FCSTD DOCUMENT  (FreeCAD 0.18R16131 (Git))
Label: Ladeflaeche
License: All rights reserved
LicenseURL: http://en.wikipedia.org/wiki/All_rights_reserved
objects: App::Part×3, Sketcher::SketchObject×3
note: 3 computed .brp shape members not serialized (recipe doc carries the construction recipe); baked Part::Feature solids carry a one-line shape summary decoded from their .brp

FEATURE [App::Part] Part
  Origin = -> Origin
FEATURE [Sketcher::SketchObject] Sketch
  sketch-geometry (292):
    g0: LineSegment StartX=-33.845 StartY=32.8586 StartZ=0 EndX=-13.845 EndY=32.8586 EndZ=0
    g1: LineSegment StartX=-33.845 StartY=32.8586 StartZ=0 EndX=-33.845 EndY=29.8586 EndZ=0
    g2: LineSegment StartX=-33.845 StartY=29.8586 StartZ=0 EndX=-43.845 EndY=29.8586 EndZ=0
    g3: LineSegment StartX=-43.845 StartY=29.8586 StartZ=0 EndX=-43.845 EndY=19.8586 EndZ=0
    g4: LineSegment StartX=-43.845 StartY=19.8586 StartZ=0 EndX=-33.845 EndY=19.8586 EndZ=0
    g5: LineSegment StartX=-33.845 StartY=19.8586 StartZ=0 EndX=-33.845 EndY=6.85863 EndZ=0
    g6: LineSegment StartX=-33.845 StartY=6.85863 StartZ=0 EndX=-13.845 EndY=6.85863 EndZ=0
    g7: LineSegment StartX=-13.845 StartY=6.85863 StartZ=0 EndX=-13.845 EndY=19.8586 EndZ=0
    g8: LineSegment StartX=-13.845 StartY=19.8586 StartZ=0 EndX=-3.84503 EndY=19.8586 EndZ=0
    g9: LineSegment StartX=-3.84503 StartY=19.8586 StartZ=0 EndX=-3.84503 EndY=29.8586 EndZ=0
    g10: LineSegment StartX=-3.84503 StartY=29.8586 StartZ=0 EndX=-13.845 EndY=29.8586 EndZ=0
    g11: LineSegment StartX=-13.845 StartY=29.8586 StartZ=0 EndX=-13.845 EndY=32.8586 EndZ=0
    g12: LineSegment StartX=-259.768 StartY=205.25 StartZ=0 EndX=-259.768 EndY=208.25 EndZ=0
    g13: LineSegment StartX=-259.768 StartY=208.25 StartZ=0 EndX=-219.768 EndY=208.25 EndZ=0
    g14: LineSegment StartX=-219.768 StartY=208.25 StartZ=0 EndX=-219.768 EndY=205.25 EndZ=0
    g15: LineSegment StartX=-219.768 StartY=205.25 StartZ=0 EndX=-179.768 EndY=205.25 EndZ=0
    g16: LineSegment StartX=-179.768 StartY=205.25 StartZ=0 EndX=-179.768 EndY=208.25 EndZ=0
    g17: LineSegment StartX=-179.768 StartY=208.25 StartZ=0 EndX=-139.768 EndY=208.25 EndZ=0
    g18: LineSegment StartX=-139.768 StartY=208.25 StartZ=0 EndX=-139.768 EndY=205.25 EndZ=0
    g19: LineSegment StartX=-139.768 StartY=205.25 StartZ=0 EndX=-99.7679 EndY=205.25 EndZ=0
    g20: LineSegment StartX=-99.7679 StartY=205.25 StartZ=0 EndX=-99.7679 EndY=208.25 EndZ=0
    g21: LineSegment StartX=-99.7679 StartY=208.25 StartZ=0 EndX=-59.7679 EndY=208.25 EndZ=0
    g22: LineSegment StartX=-59.7679 StartY=208.25 StartZ=0 EndX=-59.7679 EndY=205.25 EndZ=0
    g23: LineSegment StartX=-259.768 StartY=205.25 StartZ=0 EndX=-256.768 EndY=205.25 EndZ=0
    g24: LineSegment StartX=-256.768 StartY=205.25 StartZ=0 EndX=-256.768 EndY=175.25 EndZ=0
    g25: LineSegment StartX=-256.768 StartY=175.25 StartZ=0 EndX=-259.768 EndY=175.25 EndZ=0
    g26: LineSegment StartX=-259.768 StartY=175.25 StartZ=0 EndX=-259.768 EndY=145.25 EndZ=0
    g27: LineSegment StartX=-59.7679 StartY=205.25 StartZ=0 EndX=-62.7679 EndY=205.25 EndZ=0
    g28: LineSegment StartX=-62.7679 StartY=205.25 StartZ=0 EndX=-62.7679 EndY=175.25 EndZ=0
    g29: LineSegment StartX=-62.7679 StartY=175.25 StartZ=0 EndX=-59.7679 EndY=175.25 EndZ=0
    g30: LineSegment StartX=-59.7679 StartY=175.25 StartZ=0 EndX=-59.7679 EndY=145.25 EndZ=0
    g31: LineSegment StartX=-259.768 StartY=145.25 StartZ=0 EndX=-256.768 EndY=145.25 EndZ=0
    g32: LineSegment StartX=-256.768 StartY=145.25 StartZ=0 EndX=-256.768 EndY=115.25 EndZ=0
    g33: LineSegment StartX=-256.768 StartY=115.25 StartZ=0 EndX=-259.768 EndY=115.25 EndZ=0
    g34: LineSegment StartX=-259.768 StartY=115.25 StartZ=0 EndX=-259.768 EndY=93.2502 EndZ=0
    g35: LineSegment StartX=-259.768 StartY=93.2502 StartZ=0 EndX=-256.768 EndY=93.2502 EndZ=0
    g36: LineSegment StartX=-256.768 StartY=93.2502 StartZ=0 EndX=-256.768 EndY=63.2502 EndZ=0
    g37: LineSegment StartX=-256.768 StartY=63.2502 StartZ=0 EndX=-259.768 EndY=63.2502 EndZ=0
    g38: LineSegment StartX=-259.768 StartY=63.2502 StartZ=0 EndX=-259.768 EndY=30.1502 EndZ=0
    g39: LineSegment StartX=-259.768 StartY=30.1502 StartZ=0 EndX=-219.768 EndY=30.1502 EndZ=0
    g40: LineSegment StartX=-219.768 StartY=30.1502 StartZ=0 EndX=-219.768 EndY=33.1502 EndZ=0
    g41: LineSegment StartX=-219.768 StartY=33.1502 StartZ=0 EndX=-179.768 EndY=33.1502 EndZ=0
    g42: LineSegment StartX=-179.768 StartY=33.1502 StartZ=0 EndX=-179.768 EndY=30.1502 EndZ=0
    g43: LineSegment StartX=-179.768 StartY=30.1502 StartZ=0 EndX=-139.768 EndY=30.1502 EndZ=0
    g44: LineSegment StartX=-139.768 StartY=30.1502 StartZ=0 EndX=-139.768 EndY=33.1502 EndZ=0
    g45: LineSegment StartX=-139.768 StartY=33.1502 StartZ=0 EndX=-99.7679 EndY=33.1502 EndZ=0
    g46: LineSegment StartX=-99.7679 StartY=33.1502 StartZ=0 EndX=-99.7679 EndY=30.1502 EndZ=0
    g47: LineSegment StartX=-99.7679 StartY=30.1502 StartZ=0 EndX=-59.7679 EndY=30.1502 EndZ=0
    g48: LineSegment StartX=-59.7679 StartY=30.1502 StartZ=0 EndX=-59.7679 EndY=63.2502 EndZ=0
    g49: LineSegment StartX=-59.7679 StartY=63.2502 StartZ=0 EndX=-62.7679 EndY=63.2502 EndZ=0
    g50: LineSegment StartX=-62.7679 StartY=63.2502 StartZ=0 EndX=-62.7679 EndY=93.2502 EndZ=0
    g51: LineSegment StartX=-62.7679 StartY=93.2502 StartZ=0 EndX=-59.7679 EndY=93.2502 EndZ=0
    g52: LineSegment StartX=-59.7679 StartY=93.2502 StartZ=0 EndX=-59.7679 EndY=115.25 EndZ=0
    g53: LineSegment StartX=-59.7679 StartY=115.25 StartZ=0 EndX=-62.7679 EndY=115.25 EndZ=0
    g54: LineSegment StartX=-62.7679 StartY=115.25 StartZ=0 EndX=-62.7679 EndY=145.25 EndZ=0
    g55: LineSegment StartX=-62.7679 StartY=145.25 StartZ=0 EndX=-59.7679 EndY=145.25 EndZ=0
    g56: LineSegment StartX=-239.768 StartY=198.25 StartZ=0 EndX=-219.768 EndY=198.25 EndZ=0
    g57: LineSegment StartX=-239.768 StartY=198.25 StartZ=0 EndX=-239.768 EndY=195.15 EndZ=0
    g58: LineSegment StartX=-219.768 StartY=198.25 StartZ=0 EndX=-219.768 EndY=195.15 EndZ=0
    g59: LineSegment StartX=-239.768 StartY=195.15 StartZ=0 EndX=-219.768 EndY=195.15 EndZ=0
    g60: LineSegment StartX=-99.7679 StartY=198.25 StartZ=0 EndX=-99.7679 EndY=195.15 EndZ=0
    g61: LineSegment StartX=-99.7679 StartY=198.25 StartZ=0 EndX=-79.7679 EndY=198.25 EndZ=0
    g62: LineSegment StartX=-79.7679 StartY=198.25 StartZ=0 EndX=-79.7679 EndY=195.15 EndZ=0
    g63: LineSegment StartX=-99.7679 StartY=195.15 StartZ=0 EndX=-79.7679 EndY=195.15 EndZ=0
    g64: LineSegment StartX=-239.768 StartY=48.2502 StartZ=0 EndX=-219.768 EndY=48.2502 EndZ=0
    g65: LineSegment StartX=-219.768 StartY=48.2502 StartZ=0 EndX=-219.768 EndY=51.3502 EndZ=0
    g66: LineSegment StartX=-219.768 StartY=51.3502 StartZ=0 EndX=-239.768 EndY=51.3502 EndZ=0
    g67: LineSegment StartX=-239.768 StartY=48.2502 StartZ=0 EndX=-239.768 EndY=51.3502 EndZ=0
    g68: LineSegment StartX=-99.7679 StartY=48.2502 StartZ=0 EndX=-79.7679 EndY=48.2502 EndZ=0
    g69: LineSegment StartX=-79.7679 StartY=48.2502 StartZ=0 EndX=-79.7679 EndY=45.1502 EndZ=0
    g70: LineSegment StartX=-79.7679 StartY=45.1502 StartZ=0 EndX=-99.7679 EndY=45.1502 EndZ=0
    g71: LineSegment StartX=-99.7679 StartY=48.2502 StartZ=0 EndX=-99.7679 EndY=45.1502 EndZ=0
    g72: LineSegment StartX=-239.768 StartY=105.15 StartZ=0 EndX=-219.768 EndY=105.15 EndZ=0
    g73: LineSegment StartX=-239.768 StartY=105.15 StartZ=0 EndX=-239.768 EndY=108.25 EndZ=0
    g74: LineSegment StartX=-239.768 StartY=108.25 StartZ=0 EndX=-219.768 EndY=108.25 EndZ=0
    g75: LineSegment StartX=-219.768 StartY=108.25 StartZ=0 EndX=-219.768 EndY=105.15 EndZ=0
    g76: LineSegment StartX=-99.7679 StartY=105.15 StartZ=0 EndX=-99.7679 EndY=108.25 EndZ=0
    g77: LineSegment StartX=-99.7679 StartY=108.25 StartZ=0 EndX=-79.7679 EndY=108.25 EndZ=0
    g78: LineSegment StartX=-79.7679 StartY=108.25 StartZ=0 EndX=-79.7679 EndY=105.15 EndZ=0
    g79: LineSegment StartX=-99.7679 StartY=105.15 StartZ=0 EndX=-79.7679 EndY=105.15 EndZ=0
    g80: LineSegment StartX=-209.768 StartY=175.25 StartZ=0 EndX=-169.768 EndY=175.25 EndZ=0
    g81: LineSegment StartX=-209.768 StartY=175.25 StartZ=0 EndX=-209.768 EndY=172.25 EndZ=0
    g82: LineSegment StartX=-209.768 StartY=172.25 StartZ=0 EndX=-169.768 EndY=172.25 EndZ=0
    g83: LineSegment StartX=-169.768 StartY=175.25 StartZ=0 EndX=-169.768 EndY=172.25 EndZ=0
    g84: LineSegment StartX=-149.768 StartY=175.25 StartZ=0 EndX=-149.768 EndY=172.25 EndZ=0
    g85: LineSegment StartX=-149.768 StartY=175.25 StartZ=0 EndX=-109.768 EndY=175.25 EndZ=0
    g86: LineSegment StartX=-109.768 StartY=175.25 StartZ=0 EndX=-109.768 EndY=172.25 EndZ=0
    g87: LineSegment StartX=-149.768 StartY=172.25 StartZ=0 EndX=-109.768 EndY=172.25 EndZ=0
    g88: LineSegment StartX=-232.768 StartY=93.2502 StartZ=0 EndX=-229.768 EndY=93.2502 EndZ=0
    g89: LineSegment StartX=-232.768 StartY=93.2502 StartZ=0 EndX=-232.768 EndY=63.2502 EndZ=0
    g90: LineSegment StartX=-232.768 StartY=63.2502 StartZ=0 EndX=-229.768 EndY=63.2502 EndZ=0
    g91: LineSegment StartX=-229.768 StartY=93.2502 StartZ=0 EndX=-229.768 EndY=63.2502 EndZ=0
    g92: LineSegment StartX=-232.768 StartY=145.25 StartZ=0 EndX=-232.768 EndY=115.25 EndZ=0
    g93: LineSegment StartX=-232.768 StartY=115.25 StartZ=0 EndX=-229.768 EndY=115.25 EndZ=0
    g94: LineSegment StartX=-229.768 StartY=145.25 StartZ=0 EndX=-229.768 EndY=115.25 EndZ=0
    g95: LineSegment StartX=-232.768 StartY=145.25 StartZ=0 EndX=-229.768 EndY=145.25 EndZ=0
    g96: LineSegment StartX=-89.7679 StartY=145.25 StartZ=0 EndX=-89.7679 EndY=115.25 EndZ=0
    g97: LineSegment StartX=-89.7679 StartY=145.25 StartZ=0 EndX=-86.7679 EndY=145.25 EndZ=0
    g98: LineSegment StartX=-86.7679 StartY=145.25 StartZ=0 EndX=-86.7679 EndY=115.25 EndZ=0
    g99: LineSegment StartX=-89.7679 StartY=115.25 StartZ=0 EndX=-86.7679 EndY=115.25 EndZ=0
    g100: LineSegment StartX=-89.7679 StartY=93.2502 StartZ=0 EndX=-89.7679 EndY=63.2502 EndZ=0
    g101: LineSegment StartX=-89.7679 StartY=93.2502 StartZ=0 EndX=-86.7679 EndY=93.2502 EndZ=0
    g102: LineSegment StartX=-86.7679 StartY=93.2502 StartZ=0 EndX=-86.7679 EndY=63.2502 EndZ=0
    g103: LineSegment StartX=-89.7679 StartY=63.2502 StartZ=0 EndX=-86.7679 EndY=63.2502 EndZ=0
    g104: LineSegment StartX=-199.768 StartY=45.1502 StartZ=0 EndX=-169.768 EndY=45.1502 EndZ=0
    g105: LineSegment StartX=-199.768 StartY=45.1502 StartZ=0 EndX=-199.768 EndY=42.1502 EndZ=0
    g106: LineSegment StartX=-199.768 StartY=42.1502 StartZ=0 EndX=-169.768 EndY=42.1502 EndZ=0
    g107: LineSegment StartX=-169.768 StartY=45.1502 StartZ=0 EndX=-169.768 EndY=42.1502 EndZ=0
    g108: LineSegment StartX=-149.768 StartY=45.1502 StartZ=0 EndX=-149.768 EndY=42.1502 EndZ=0
    g109: LineSegment StartX=-149.768 StartY=45.1502 StartZ=0 EndX=-119.768 EndY=45.1502 EndZ=0
    g110: LineSegment StartX=-149.768 StartY=42.1502 StartZ=0 EndX=-119.768 EndY=42.1502 EndZ=0
    g111: LineSegment StartX=-119.768 StartY=45.1502 StartZ=0 EndX=-119.768 EndY=42.1502 EndZ=0
    g112: LineSegment StartX=-240.224 StartY=222.745 StartZ=0 EndX=-220.224 EndY=222.745 EndZ=0
    g113: LineSegment StartX=-220.224 StartY=222.745 StartZ=0 EndX=-220.224 EndY=219.745 EndZ=0
    g114: LineSegment StartX=-220.224 StartY=219.745 StartZ=0 EndX=-180.224 EndY=219.745 EndZ=0
    g115: LineSegment StartX=-180.224 StartY=219.745 StartZ=0 EndX=-180.224 EndY=222.745 EndZ=0
    g116: LineSegment StartX=-180.224 StartY=222.745 StartZ=0 EndX=-140.224 EndY=222.745 EndZ=0
    g117: LineSegment StartX=-140.224 StartY=222.745 StartZ=0 EndX=-140.224 EndY=219.745 EndZ=0
    g118: LineSegment StartX=-140.224 StartY=219.745 StartZ=0 EndX=-100.224 EndY=219.745 EndZ=0
    g119: LineSegment StartX=-100.224 StartY=219.745 StartZ=0 EndX=-100.224 EndY=222.745 EndZ=0
    g120: LineSegment StartX=-100.224 StartY=222.745 StartZ=0 EndX=-63.2242 EndY=222.745 EndZ=0
    g121: LineSegment StartX=-63.2242 StartY=222.745 StartZ=0 EndX=-63.2242 EndY=262.745 EndZ=0
    g122: LineSegment StartX=-60.2242 StartY=262.745 StartZ=0 EndX=-63.2242 EndY=262.745 EndZ=0
    g123: LineSegment StartX=-60.2242 StartY=262.745 StartZ=0 EndX=-60.2242 EndY=292.745 EndZ=0
    g124: LineSegment StartX=-63.2242 StartY=292.745 StartZ=0 EndX=-60.2242 EndY=292.745 EndZ=0
    g125: LineSegment StartX=-63.2242 StartY=292.745 StartZ=0 EndX=-63.2242 EndY=322.745 EndZ=0
    g126: LineSegment StartX=-60.2242 StartY=322.745 StartZ=0 EndX=-63.2242 EndY=322.745 EndZ=0
    g127: LineSegment StartX=-60.2242 StartY=322.745 StartZ=0 EndX=-60.2242 EndY=352.745 EndZ=0
    g128: LineSegment StartX=-63.2242 StartY=352.745 StartZ=0 EndX=-60.2242 EndY=352.745 EndZ=0
    g129: LineSegment StartX=-63.2242 StartY=352.745 StartZ=0 EndX=-63.2242 EndY=382.745 EndZ=0
    g130: LineSegment StartX=-63.2242 StartY=382.745 StartZ=0 EndX=-83.2242 EndY=382.745 EndZ=0
    g131: LineSegment StartX=-83.2242 StartY=382.745 StartZ=0 EndX=-83.2242 EndY=379.745 EndZ=0
    g132: LineSegment StartX=-237.224 StartY=379.745 StartZ=0 EndX=-237.224 EndY=382.745 EndZ=0
    g133: LineSegment StartX=-237.224 StartY=382.745 StartZ=0 EndX=-257.224 EndY=382.745 EndZ=0
    g134: LineSegment StartX=-257.224 StartY=382.745 StartZ=0 EndX=-257.224 EndY=352.745 EndZ=0
    g135: LineSegment StartX=-260.224 StartY=352.745 StartZ=0 EndX=-257.224 EndY=352.745 EndZ=0
    g136: LineSegment StartX=-260.224 StartY=352.745 StartZ=0 EndX=-260.224 EndY=322.745 EndZ=0
    g137: LineSegment StartX=-257.224 StartY=322.745 StartZ=0 EndX=-260.224 EndY=322.745 EndZ=0
    g138: LineSegment StartX=-257.224 StartY=322.745 StartZ=0 EndX=-257.224 EndY=292.745 EndZ=0
    g139: LineSegment StartX=-260.224 StartY=292.745 StartZ=0 EndX=-257.224 EndY=292.745 EndZ=0
    g140: LineSegment StartX=-260.224 StartY=292.745 StartZ=0 EndX=-260.224 EndY=262.745 EndZ=0
    g141: LineSegment StartX=-217.768 StartY=195.25 StartZ=0 EndX=-217.768 EndY=185.25 EndZ=0
    g142: LineSegment StartX=-217.768 StartY=195.25 StartZ=0 EndX=-214.768 EndY=195.25 EndZ=0
    g143: LineSegment StartX=-214.768 StartY=195.25 StartZ=0 EndX=-214.768 EndY=185.25 EndZ=0
    g144: LineSegment StartX=-217.768 StartY=185.25 StartZ=0 EndX=-214.768 EndY=185.25 EndZ=0
    g145: LineSegment StartX=-104.768 StartY=195.25 StartZ=0 EndX=-101.768 EndY=195.25 EndZ=0
    g146: LineSegment StartX=-104.768 StartY=195.25 StartZ=0 EndX=-104.768 EndY=185.25 EndZ=0
    g147: LineSegment StartX=-104.768 StartY=185.25 StartZ=0 EndX=-101.768 EndY=185.25 EndZ=0
    g148: LineSegment StartX=-101.768 StartY=195.25 StartZ=0 EndX=-101.768 EndY=185.25 EndZ=0
    g149: LineSegment StartX=-255.939 StartY=410.901 StartZ=0 EndX=-235.939 EndY=410.901 EndZ=0
    g150: LineSegment StartX=-235.939 StartY=410.901 StartZ=0 EndX=-235.939 EndY=407.901 EndZ=0
    g151: LineSegment StartX=-235.939 StartY=407.901 StartZ=0 EndX=-213.939 EndY=407.901 EndZ=0
    g152: LineSegment StartX=-213.939 StartY=443.901 StartZ=0 EndX=-235.93 EndY=443.901 EndZ=0
    g153: LineSegment StartX=-235.93 StartY=443.901 StartZ=0 EndX=-235.939 EndY=440.901 EndZ=0
    g154: LineSegment StartX=-235.939 StartY=440.901 StartZ=0 EndX=-255.908 EndY=440.901 EndZ=0
    g155: LineSegment StartX=-255.908 StartY=440.901 StartZ=0 EndX=-255.939 EndY=430.901 EndZ=0
    g156: LineSegment StartX=-255.939 StartY=430.901 StartZ=0 EndX=-258.939 EndY=430.901 EndZ=0
    g157: LineSegment StartX=-258.939 StartY=430.901 StartZ=0 EndX=-258.97 EndY=420.901 EndZ=0
    g158: LineSegment StartX=-258.97 StartY=420.901 StartZ=0 EndX=-255.939 EndY=420.901 EndZ=0
    g159: LineSegment StartX=-255.939 StartY=420.901 StartZ=0 EndX=-255.939 EndY=410.901 EndZ=0
    g160: LineSegment StartX=-274.181 StartY=220.034 StartZ=0 EndX=-274.181 EndY=223.034 EndZ=0
    g161: LineSegment StartX=-274.181 StartY=223.034 StartZ=0 EndX=-271.181 EndY=223.034 EndZ=0
    g162: LineSegment StartX=-274.181 StartY=220.034 StartZ=0 EndX=-304.181 EndY=220.034 EndZ=0
    g163: LineSegment StartX=-304.181 StartY=220.034 StartZ=0 EndX=-304.181 EndY=223.034 EndZ=0
    g164: LineSegment StartX=-304.181 StartY=223.034 StartZ=0 EndX=-307.181 EndY=223.034 EndZ=0
    g165: LineSegment StartX=-271.181 StartY=223.034 StartZ=0 EndX=-271.181 EndY=263.034 EndZ=0
    g166: LineSegment StartX=-271.181 StartY=263.034 StartZ=0 EndX=-274.181 EndY=263.034 EndZ=0
    g167: LineSegment StartX=-274.181 StartY=263.034 StartZ=0 EndX=-274.181 EndY=293.034 EndZ=0
    g168: LineSegment StartX=-274.181 StartY=293.034 StartZ=0 EndX=-271.181 EndY=293.034 EndZ=0
    g169: LineSegment StartX=-271.181 StartY=293.034 StartZ=0 EndX=-271.181 EndY=323.034 EndZ=0
    g170: LineSegment StartX=-271.181 StartY=323.034 StartZ=0 EndX=-274.181 EndY=323.034 EndZ=0
    g171: LineSegment StartX=-274.181 StartY=323.034 StartZ=0 EndX=-274.181 EndY=353.034 EndZ=0
    g172: LineSegment StartX=-274.181 StartY=353.034 StartZ=0 EndX=-271.181 EndY=353.034 EndZ=0
    g173: LineSegment StartX=-271.181 StartY=353.034 StartZ=0 EndX=-271.181 EndY=383.034 EndZ=0
    g174: LineSegment StartX=-271.181 StartY=383.034 StartZ=0 EndX=-284.181 EndY=383.034 EndZ=0
    g175: LineSegment StartX=-284.181 StartY=383.034 StartZ=0 EndX=-284.181 EndY=380.034 EndZ=0
    g176: LineSegment StartX=-284.181 StartY=380.034 StartZ=0 EndX=-294.181 EndY=380.034 EndZ=0
    g177: LineSegment StartX=-294.181 StartY=380.034 StartZ=0 EndX=-294.181 EndY=383.034 EndZ=0
    g178: LineSegment StartX=-294.181 StartY=383.034 StartZ=0 EndX=-307.181 EndY=383.034 EndZ=0
    g179: LineSegment StartX=-307.181 StartY=383.034 StartZ=0 EndX=-307.181 EndY=353.034 EndZ=0
    g180: LineSegment StartX=-307.181 StartY=353.034 StartZ=0 EndX=-304.181 EndY=353.034 EndZ=0
    g181: LineSegment StartX=-304.181 StartY=353.034 StartZ=0 EndX=-304.181 EndY=323.034 EndZ=0
    g182: LineSegment StartX=-304.181 StartY=323.034 StartZ=0 EndX=-307.181 EndY=323.034 EndZ=0
    g183: LineSegment StartX=-307.181 StartY=323.034 StartZ=0 EndX=-307.181 EndY=293.034 EndZ=0
    g184: LineSegment StartX=-307.181 StartY=293.034 StartZ=0 EndX=-304.181 EndY=293.034 EndZ=0
    g185: LineSegment StartX=-304.181 StartY=293.034 StartZ=0 EndX=-304.181 EndY=263.034 EndZ=0
    g186: LineSegment StartX=-304.181 StartY=263.034 StartZ=0 EndX=-307.181 EndY=263.034 EndZ=0
    g187: LineSegment StartX=-307.181 StartY=263.034 StartZ=0 EndX=-307.181 EndY=223.034 EndZ=0
    g188: LineSegment StartX=-327.592 StartY=380.152 StartZ=0 EndX=-327.592 EndY=223.152 EndZ=0
    g189: LineSegment StartX=-327.592 StartY=223.152 StartZ=0 EndX=-337.592 EndY=223.152 EndZ=0
    g190: LineSegment StartX=-337.592 StartY=223.152 StartZ=0 EndX=-337.592 EndY=220.152 EndZ=0
    g191: LineSegment StartX=-337.592 StartY=220.152 StartZ=0 EndX=-347.592 EndY=220.152 EndZ=0
    g192: LineSegment StartX=-347.592 StartY=220.152 StartZ=0 EndX=-347.592 EndY=223.152 EndZ=0
    g193: LineSegment StartX=-347.592 StartY=223.152 StartZ=0 EndX=-357.592 EndY=223.152 EndZ=0
    g194: LineSegment StartX=-357.592 StartY=223.152 StartZ=0 EndX=-357.592 EndY=380.224 EndZ=0
    g195: LineSegment StartX=-348.457 StartY=27.4619 StartZ=0 EndX=-348.457 EndY=30.4619 EndZ=0
    g196: LineSegment StartX=-348.457 StartY=27.4619 StartZ=0 EndX=-388.457 EndY=27.4619 EndZ=0
    g197: LineSegment StartX=-388.457 StartY=27.4619 StartZ=0 EndX=-388.457 EndY=30.4619 EndZ=0
    g198: LineSegment StartX=-388.457 StartY=30.4619 StartZ=0 EndX=-408.457 EndY=30.4619 EndZ=0
    g199: LineSegment StartX=-408.457 StartY=30.4619 StartZ=0 EndX=-408.457 EndY=27.4619 EndZ=0
    g200: LineSegment StartX=-408.457 StartY=27.4619 StartZ=0 EndX=-448.457 EndY=27.4619 EndZ=0
    g201: LineSegment StartX=-448.457 StartY=27.4619 StartZ=0 EndX=-448.457 EndY=30.4619 EndZ=0
    g202: LineSegment StartX=-471.457 StartY=70.4619 StartZ=0 EndX=-498.457 EndY=70.4619 EndZ=0
    g203: LineSegment StartX=-348.457 StartY=30.4619 StartZ=0 EndX=-301.456 EndY=30.4619 EndZ=0
    g204: LineSegment StartX=-301.456 StartY=30.4619 StartZ=0 EndX=-301.456 EndY=70.4619 EndZ=0
    g205: LineSegment StartX=-301.456 StartY=70.4619 StartZ=0 EndX=-298.456 EndY=70.4619 EndZ=0
    g206: LineSegment StartX=-298.456 StartY=70.4619 StartZ=0 EndX=-298.456 EndY=100.462 EndZ=0
    g207: LineSegment StartX=-298.456 StartY=100.462 StartZ=0 EndX=-301.456 EndY=100.462 EndZ=0
    g208: LineSegment StartX=-301.456 StartY=100.462 StartZ=0 EndX=-301.456 EndY=130.462 EndZ=0
    g209: LineSegment StartX=-301.456 StartY=130.462 StartZ=0 EndX=-298.456 EndY=130.462 EndZ=0
    g210: LineSegment StartX=-298.456 StartY=130.462 StartZ=0 EndX=-298.456 EndY=160.462 EndZ=0
    g211: LineSegment StartX=-298.456 StartY=160.462 StartZ=0 EndX=-301.456 EndY=160.462 EndZ=0
    g212: LineSegment StartX=-301.456 StartY=160.462 StartZ=0 EndX=-301.456 EndY=190.462 EndZ=0
    g213: LineSegment StartX=-498.457 StartY=70.4619 StartZ=0 EndX=-498.457 EndY=100.462 EndZ=0
    g214: LineSegment StartX=-498.457 StartY=100.462 StartZ=0 EndX=-495.457 EndY=100.462 EndZ=0
    g215: LineSegment StartX=-495.457 StartY=100.462 StartZ=0 EndX=-495.456 EndY=130.462 EndZ=0
    g216: LineSegment StartX=-495.456 StartY=130.462 StartZ=0 EndX=-498.456 EndY=130.462 EndZ=0
    g217: LineSegment StartX=-498.456 StartY=130.462 StartZ=0 EndX=-498.456 EndY=160.462 EndZ=0
    g218: LineSegment StartX=-498.456 StartY=160.462 StartZ=0 EndX=-495.456 EndY=160.462 EndZ=0
    g219: LineSegment StartX=-495.456 StartY=160.462 StartZ=0 EndX=-495.456 EndY=190.462 EndZ=0
    g220: LineSegment StartX=-453.456 StartY=160.462 StartZ=0 EndX=-343.456 EndY=160.462 EndZ=0
    g221: LineSegment StartX=-343.456 StartY=160.462 StartZ=0 EndX=-343.456 EndY=187.462 EndZ=0
    g222: Circle CenterX=-229.224 CenterY=244.745 CenterZ=0 NormalX=0 NormalY=0 NormalZ=1 AngleXU=0 Radius=10
    g223: Circle CenterX=-29.845 CenterY=15.2586 CenterZ=0 NormalX=0 NormalY=0 NormalZ=1 AngleXU=0 Radius=1.6
    g224: Circle CenterX=-17.845 CenterY=15.2586 CenterZ=0 NormalX=0 NormalY=0 NormalZ=1 AngleXU=0 Radius=1.6
    g225: LineSegment StartX=-495.456 StartY=190.462 StartZ=0 EndX=-475.456 EndY=190.462 EndZ=0
    g226: LineSegment StartX=-475.456 StartY=190.462 StartZ=0 EndX=-475.456 EndY=187.462 EndZ=0
    g227: LineSegment StartX=-475.456 StartY=187.462 StartZ=0 EndX=-457.456 EndY=187.462 EndZ=0
    g228: LineSegment StartX=-301.456 StartY=190.462 StartZ=0 EndX=-321.456 EndY=190.462 EndZ=0
    g229: LineSegment StartX=-321.456 StartY=190.462 StartZ=0 EndX=-321.456 EndY=187.462 EndZ=0
    g230: LineSegment StartX=-321.456 StartY=187.462 StartZ=0 EndX=-343.456 EndY=187.462 EndZ=0
    g231: Circle CenterX=-462.857 CenterY=55.4619 CenterZ=0 NormalX=0 NormalY=0 NormalZ=1 AngleXU=0 Radius=1.6
    g232: Circle CenterX=-444.957 CenterY=55.4619 CenterZ=0 NormalX=0 NormalY=0 NormalZ=1 AngleXU=0 Radius=1.6
    g233: Circle CenterX=-351.957 CenterY=55.4619 CenterZ=0 NormalX=0 NormalY=0 NormalZ=1 AngleXU=0 Radius=1.6
    g234: Circle CenterX=-334.057 CenterY=55.4619 CenterZ=0 NormalX=0 NormalY=0 NormalZ=1 AngleXU=0 Radius=1.6
    g235: LineSegment StartX=-464.702 StartY=257.339 StartZ=0 EndX=-464.702 EndY=260.339 EndZ=0
    g236: LineSegment StartX=-464.702 StartY=260.339 StartZ=0 EndX=-415.702 EndY=260.339 EndZ=0
    g237: LineSegment StartX=-415.702 StartY=260.339 StartZ=0 EndX=-415.702 EndY=257.339 EndZ=0
    g238: LineSegment StartX=-415.702 StartY=257.339 StartZ=0 EndX=-385.702 EndY=257.339 EndZ=0
    g239: LineSegment StartX=-385.702 StartY=257.339 StartZ=0 EndX=-385.702 EndY=224.339 EndZ=0
    g240: LineSegment StartX=-385.702 StartY=224.339 StartZ=0 EndX=-494.702 EndY=224.339 EndZ=0
    g241: LineSegment StartX=-494.702 StartY=224.339 StartZ=0 EndX=-494.702 EndY=257.339 EndZ=0
    g242: LineSegment StartX=-494.702 StartY=257.339 StartZ=0 EndX=-464.702 EndY=257.339 EndZ=0
    g243: LineSegment StartX=-502.615 StartY=306.597 StartZ=0 EndX=-393.615 EndY=306.597 EndZ=0
    g244: LineSegment StartX=-393.631 StartY=276.597 StartZ=0 EndX=-423.631 EndY=276.597 EndZ=0
    g245: LineSegment StartX=-423.631 StartY=276.597 StartZ=0 EndX=-423.631 EndY=279.597 EndZ=0
    g246: LineSegment StartX=-423.631 StartY=279.597 StartZ=0 EndX=-472.615 EndY=279.597 EndZ=0
    g247: LineSegment StartX=-472.615 StartY=279.597 StartZ=0 EndX=-472.615 EndY=276.597 EndZ=0
    g248: LineSegment StartX=-472.615 StartY=276.597 StartZ=0 EndX=-502.615 EndY=276.597 EndZ=0
    g249: LineSegment StartX=-471.457 StartY=70.4619 StartZ=0 EndX=-471.457 EndY=30.4619 EndZ=0
    g250: LineSegment StartX=-471.457 StartY=30.4619 StartZ=0 EndX=-448.457 EndY=30.4619 EndZ=0
    g251: Circle CenterX=-407.406 CenterY=148.462 CenterZ=0 NormalX=0 NormalY=0 NormalZ=1 AngleXU=0 Radius=1.6
    g252: Circle CenterX=-389.506 CenterY=148.462 CenterZ=0 NormalX=0 NormalY=0 NormalZ=1 AngleXU=0 Radius=1.6
    g253: LineSegment StartX=-357.592 StartY=380.224 StartZ=0 EndX=-347.592 EndY=380.224 EndZ=0
    g254: LineSegment StartX=-347.592 StartY=380.224 StartZ=0 EndX=-347.592 EndY=383.224 EndZ=0
    g255: LineSegment StartX=-347.592 StartY=383.224 StartZ=0 EndX=-337.592 EndY=383.224 EndZ=0
    g256: LineSegment StartX=-337.592 StartY=383.224 StartZ=0 EndX=-337.592 EndY=380.152 EndZ=0
    g257: LineSegment StartX=-337.592 StartY=380.152 StartZ=0 EndX=-327.592 EndY=380.152 EndZ=0
    g258: LineSegment StartX=-213.939 StartY=443.901 StartZ=0 EndX=-213.939 EndY=430.901 EndZ=0
    g259: LineSegment StartX=-213.939 StartY=430.901 StartZ=0 EndX=-216.939 EndY=430.901 EndZ=0
    g260: LineSegment StartX=-216.939 StartY=430.901 StartZ=0 EndX=-216.939 EndY=420.901 EndZ=0
    g261: LineSegment StartX=-216.939 StartY=420.901 StartZ=0 EndX=-213.939 EndY=420.901 EndZ=0
    g262: LineSegment StartX=-213.939 StartY=420.901 StartZ=0 EndX=-213.939 EndY=407.901 EndZ=0
    g263: LineSegment StartX=-237.224 StartY=379.745 StartZ=0 EndX=-83.2242 EndY=379.745 EndZ=0
    g264: LineSegment StartX=-260.224 StartY=262.745 StartZ=0 EndX=-240.224 EndY=262.745 EndZ=0
    g265: LineSegment StartX=-240.224 StartY=262.745 StartZ=0 EndX=-240.224 EndY=222.745 EndZ=0
    g266: Circle CenterX=-457.065 CenterY=296.597 CenterZ=0 NormalX=0 NormalY=0 NormalZ=1 AngleXU=0 Radius=1.6
    g267: Circle CenterX=-439.165 CenterY=296.597 CenterZ=0 NormalX=0 NormalY=0 NormalZ=1 AngleXU=0 Radius=1.6
    g268: LineSegment StartX=-393.631 StartY=276.597 StartZ=0 EndX=-393.631 EndY=276.597 EndZ=0
    g269: LineSegment StartX=-393.615 StartY=306.597 StartZ=0 EndX=-393.631 EndY=276.597 EndZ=0
    g270: LineSegment StartX=-457.456 StartY=187.462 StartZ=0 EndX=-457.456 EndY=182.462 EndZ=0
    g271: LineSegment StartX=-457.456 StartY=182.462 StartZ=0 EndX=-453.456 EndY=182.462 EndZ=0
    g272: LineSegment StartX=-453.456 StartY=182.462 StartZ=0 EndX=-453.456 EndY=160.462 EndZ=0
    g273: LineSegment StartX=-189.038 StartY=431.177 StartZ=0 EndX=-189.038 EndY=421.177 EndZ=0
    g274: LineSegment StartX=-189.038 StartY=431.177 StartZ=0 EndX=-186.038 EndY=431.177 EndZ=0
    g275: LineSegment StartX=-186.038 StartY=431.177 StartZ=0 EndX=-186.038 EndY=441.177 EndZ=0
    g276: LineSegment StartX=-186.038 StartY=441.177 StartZ=0 EndX=-166.038 EndY=441.177 EndZ=0
    g277: LineSegment StartX=-166.038 StartY=441.177 StartZ=0 EndX=-166.038 EndY=444.177 EndZ=0
    g278: LineSegment StartX=-166.038 StartY=444.177 StartZ=0 EndX=-144.038 EndY=444.177 EndZ=0
    g279: LineSegment StartX=-144.038 StartY=444.177 StartZ=0 EndX=-144.038 EndY=431.177 EndZ=0
    g280: LineSegment StartX=-144.038 StartY=431.177 StartZ=0 EndX=-147.038 EndY=431.177 EndZ=0
    g281: LineSegment StartX=-147.038 StartY=431.177 StartZ=0 EndX=-147.038 EndY=421.177 EndZ=0
    g282: LineSegment StartX=-147.038 StartY=421.177 StartZ=0 EndX=-144.038 EndY=421.177 EndZ=0
    g283: LineSegment StartX=-144.038 StartY=421.177 StartZ=0 EndX=-144.038 EndY=411.177 EndZ=0
    g284: LineSegment StartX=-144.038 StartY=411.177 StartZ=0 EndX=-150.038 EndY=411.177 EndZ=0
    g285: LineSegment StartX=-150.038 StartY=411.177 StartZ=0 EndX=-150.038 EndY=408.177 EndZ=0
    g286: LineSegment StartX=-150.038 StartY=408.177 StartZ=0 EndX=-166.038 EndY=408.177 EndZ=0
    g287: LineSegment StartX=-166.038 StartY=408.177 StartZ=0 EndX=-166.038 EndY=411.177 EndZ=0
    g288: LineSegment StartX=-166.038 StartY=411.177 StartZ=0 EndX=-186.038 EndY=411.177 EndZ=0
    g289: LineSegment StartX=-186.038 StartY=411.177 StartZ=0 EndX=-186.038 EndY=421.177 EndZ=0
    g290: LineSegment StartX=-189.038 StartY=421.177 StartZ=0 EndX=-186.038 EndY=421.177 EndZ=0
    g291: LineSegment StartX=-504.549 StartY=279.826 StartZ=0 EndX=-502.615 EndY=276.597 EndZ=0
  constraints (850):
    c: Coincident(g0,g1)
    c: Coincident(g0,g11)
    c: Coincident(g11,g10)
    c: Coincident(g10,g9)
    c: Coincident(g8,g9)
    c: Coincident(g8,g7)
    c: Coincident(g7,g6)
    c: Coincident(g5,g6)
    c: Coincident(g5,g4)
    c: Coincident(g4,g3)
    c: Coincident(g2,g3)
    c: Coincident(g2,g1)
    c: Angle(g6) = 0
    c: Perpendicular(g7,g6)
    c: Parallel(g6,g4)
    c: Parallel(g4,g8)
    c: Parallel(g8,g10)
    c: Parallel(g10,g2)
    c: Parallel(g2,g0)
    c: Parallel(g7,g5)
    c: Parallel(g5,g3)
    c: Parallel(g3,g9)
    c: Parallel(g9,g11)
    c: Parallel(g11,g1)
    c: DistanceY(g1,g10) = 0
    c: DistanceY(g4,g7) = 0
    c: DistanceX(g10,g7) = 0
    c: DistanceX(g1,g4) = 0
    c: DistanceY(g11,g11) = 3
    c: DistanceX(g0,g0) = 20
    c: DistanceX(g10,g10) = 10
    c: DistanceX(g2,g2) = 10
    c: DistanceY(g7,g7) = 13
    c: DistanceY(g9,g9) = 10
    c: Coincident(g41,g40)
    c: Coincident(g40,g39)
    c: Coincident(g39,g38)
    c: Coincident(g37,g38)
    c: Coincident(g37,g36)
    c: Coincident(g35,g36)
    c: Coincident(g35,g34)
    c: Coincident(g33,g34)
    c: Coincident(g33,g32)
    c: Coincident(g31,g32)
    c: Coincident(g31,g26)
    c: Coincident(g25,g26)
    c: Coincident(g24,g25)
    c: Coincident(g23,g24)
    c: Coincident(g23,g12)
    c: Coincident(g13,g12)
    c: Coincident(g13,g14)
    c: Coincident(g14,g15)
    c: Coincident(g16,g15)
    c: Coincident(g16,g17)
    c: Coincident(g18,g17)
    c: Coincident(g18,g19)
    c: Coincident(g19,g20)
    c: Coincident(g20,g21)
    c: Coincident(g22,g21)
    c: Coincident(g22,g27)
    c: Coincident(g27,g28)
    c: Coincident(g29,g28)
    c: Coincident(g29,g30)
    c: Coincident(g55,g30)
    c: Coincident(g55,g54)
    c: Coincident(g53,g54)
    c: Coincident(g53,g52)
    c: Coincident(g51,g52)
    c: Coincident(g51,g50)
    c: Coincident(g49,g50)
    c: Coincident(g49,g48)
    c: Coincident(g48,g47)
    c: Coincident(g46,g47)
    c: Coincident(g46,g45)
    c: Coincident(g44,g45)
    c: Coincident(g44,g43)
    c: Coincident(g42,g43)
    c: Coincident(g42,g41)
    c: Angle(g45) = 0
    c: Perpendicular(g50,g45)
    c: Parallel(g45,g47)
    c: Parallel(g47,g49)
    c: Parallel(g49,g43)
    c: Parallel(g43,g41)
    c: Parallel(g41,g39)
    c: Parallel(g39,g37)
    c: Parallel(g37,g35)
    c: Parallel(g35,g33)
    c: Parallel(g33,g31)
    c: Parallel(g31,g25)
    c: Parallel(g25,g23)
    c: Parallel(g23,g13)
    c: Parallel(g13,g15)
    c: Parallel(g15,g17)
    c: Parallel(g17,g19)
    c: Parallel(g19,g21)
    c: Parallel(g21,g27)
    c: Parallel(g27,g29)
    c: Parallel(g29,g55)
    c: Parallel(g55,g53)
    c: Parallel(g53,g51)
    c: Parallel(g50,g48)
    c: Parallel(g48,g46)
    c: Parallel(g46,g44)
    c: Parallel(g44,g42)
    c: Parallel(g42,g40)
    c: Parallel(g40,g38)
    c: Parallel(g38,g36)
    c: Parallel(g36,g34)
    c: Parallel(g34,g32)
    c: Parallel(g32,g26)
    c: Parallel(g26,g24)
    c: Parallel(g24,g12)
    c: Parallel(g12,g14)
    c: Parallel(g14,g16)
    c: Parallel(g16,g18)
    c: Parallel(g18,g20)
    c: Parallel(g20,g22)
    c: Parallel(g22,g28)
    c: Parallel(g28,g30)
    c: Parallel(g30,g54)
    c: Parallel(g54,g52)
    c: DistanceY(g18,g15) = 0
    c: DistanceY(g23,g14) = 0
    c: DistanceY(g27,g19) = 0
    c: DistanceY(g41,g44) = 0
    c: DistanceX(g24,g31) = 0
    c: DistanceX(g32,g35) = 0
    c: DistanceX(g53,g50) = 0
    c: DistanceX(g28,g54) = 0
    c: DistanceY(g40,g40) = 3
    c: DistanceY(g42,g42) = 3
    c: DistanceY(g46,g46) = 3
    c: DistanceX(g49,g49) = 3
    c: DistanceX(g37,g37) = 3
    c: DistanceX(g35,g35) = 3
    c: DistanceX(g53,g53) = 3
    c: DistanceX(g29,g29) = 3
    c: DistanceX(g25,g25) = 3
    c: DistanceX(g23,g23) = 3
    c: DistanceY(g12,g12) = 3
    c: DistanceY(g18,g18) = 3
    c: DistanceY(g22,g22) = 3
    c: DistanceX(g27,g27) = 3
    c: DistanceX(g13,g13) = 40
    c: DistanceX(g15,g15) = 40
    c: DistanceX(g17,g17) = 40
    c: DistanceX(g19,g19) = 40
    c: DistanceX(g21,g21) = 40
    c: DistanceY(g28,g28) = 30
    c: DistanceY(g24,g24) = 30
    c: DistanceX(g39,g39) = 40
    c: DistanceX(g41,g41) = 40
    c: DistanceX(g43,g43) = 40
    c: DistanceX(g45,g45) = 40
    c: DistanceY(g38,g12) = 178.1
    c: DistanceY(g26,g26) = 30
    c: DistanceY(g30,g30) = 30
    c: DistanceY(g38,g38) = 33.1
    c: DistanceY(g48,g48) = 33.1
    c: DistanceY(g34,g34) = 22
    c: DistanceY(g32,g32) = 30
    c: DistanceY(g54,g54) = 30
    c: DistanceY(g52,g52) = 22
    c: Coincident(g57,g59)
    c: Coincident(g57,g56)
    c: Coincident(g58,g56)
    c: Coincident(g58,g59)
    c: Coincident(g60,g63)
    c: Coincident(g60,g61)
    c: Coincident(g62,g61)
    c: Coincident(g62,g63)
    c: Coincident(g75,g74)
    c: Coincident(g75,g72)
    c: Coincident(g73,g72)
    c: Coincident(g73,g74)
    c: Coincident(g65,g64)
    c: Coincident(g65,g66)
    c: Coincident(g66,g67)
    c: Coincident(g64,g67)
    c: Coincident(g76,g77)
    c: Coincident(g78,g77)
    c: Coincident(g78,g79)
    c: Coincident(g76,g79)
    c: Coincident(g68,g71)
    c: Coincident(g68,g69)
    c: Coincident(g70,g69)
    c: Coincident(g70,g71)
    c: Parallel(g59,g56)
    c: Parallel(g56,g13)
    c: Parallel(g13,g61)
    c: Parallel(g61,g63)
    c: Parallel(g63,g77)
    c: Parallel(g77,g79)
    c: Parallel(g79,g74)
    c: Parallel(g74,g72)
    c: Parallel(g72,g64)
    c: Parallel(g64,g66)
    c: Parallel(g66,g68)
    c: Parallel(g68,g70)
    c: Parallel(g57,g24)
    c: Parallel(g24,g58)
    c: Parallel(g58,g60)
    c: Parallel(g60,g62)
    c: Parallel(g62,g73)
    c: Parallel(g73,g75)
    c: Parallel(g75,g76)
    c: Parallel(g76,g78)
    c: Parallel(g78,g69)
    c: Parallel(g69,g71)
    c: Parallel(g71,g65)
    c: Parallel(g65,g67)
    c: DistanceY(g57,g57) = 3.1
    c: Equal(g57,g60)
    c: Equal(g60,g73)
    c: Equal(g73,g67)
    c: Equal(g67,g76)
    c: Equal(g76,g71)
    c: Equal(g56,g61)
    c: Equal(g61,g77)
    c: Equal(g77,g74)
    c: Equal(g74,g64)
    c: Equal(g64,g68)
    c: DistanceX(g12,g56) = 20
    c: DistanceY(g56,g12) = 10
    c: DistanceX(g61,g21) = 20
    c: DistanceY(g61,g21) = 10
    c: DistanceY(g64,g73) = 60
    c: DistanceY(g68,g77) = 60
    c: DistanceY(g73,g56) = 90
    c: DistanceY(g76,g60) = 90
    c: DistanceX(g73,g57) = 0
    c: DistanceX(g72,g66) = 0
    c: DistanceX(g62,g77) = 0
    c: DistanceX(g78,g68) = 0
    c: Coincident(g87,g84)
    c: Coincident(g85,g84)
    c: Coincident(g85,g86)
    c: Coincident(g87,g86)
    c: Coincident(g82,g83)
    c: Coincident(g80,g83)
    c: Coincident(g80,g81)
    c: Coincident(g82,g81)
    c: Parallel(g86,g84)
    c: Parallel(g84,g83)
    c: Parallel(g83,g81)
    c: Parallel(g81,g28)
    c: Parallel(g85,g87)
    c: Parallel(g87,g82)
    c: Parallel(g82,g80)
    c: Parallel(g80,g19)
    c: DistanceY(g86,g86) = 3
    c: DistanceY(g83,g83) = 3
    c: DistanceY(g28,g85) = 0
    c: DistanceY(g28,g80) = 0
    c: DistanceX(g56,g56) = 20
    c: DistanceX(g85,g85) = 40
    c: DistanceX(g80,g80) = 40
    c: DistanceX(g85,g60) = 10
    c: DistanceX(g58,g80) = 10
    c: Coincident(g89,g90)
    c: Coincident(g91,g90)
    c: Coincident(g91,g88)
    c: Coincident(g89,g88)
    c: Coincident(g92,g95)
    c: Coincident(g94,g95)
    c: Coincident(g94,g93)
    c: Coincident(g93,g92)
    c: Coincident(g96,g99)
    c: Coincident(g98,g99)
    c: Coincident(g98,g97)
    c: Coincident(g96,g97)
    c: Coincident(g100,g101)
    c: Coincident(g102,g101)
    c: Coincident(g102,g103)
    c: Coincident(g100,g103)
    c: Parallel(g89,g91)
    c: Parallel(g91,g92)
    c: Parallel(g92,g94)
    c: Parallel(g94,g96)
    c: Parallel(g96,g98)
    c: Parallel(g98,g100)
    c: Parallel(g100,g102)
    c: Parallel(g102,g36)
    c: Parallel(g90,g93)
    c: Parallel(g93,g99)
    c: Parallel(g99,g103)
    c: Parallel(g103,g101)
    c: Parallel(g101,g97)
    c: Parallel(g97,g95)
    c: Parallel(g95,g88)
    c: Parallel(g88,g72)
    c: DistanceX(g88,g88) = 3
    c: Equal(g88,g95)
    c: Equal(g95,g97)
    c: Equal(g97,g101)
    c: DistanceY(g91,g91) = 30
    c: Equal(g91,g94)
    c: Equal(g94,g98)
    c: Equal(g98,g102)
    c: DistanceY(g88,g35) = 0
    c: DistanceY(g101,g50) = 0
    c: DistanceY(g31,g92) = 0
    c: DistanceY(g54,g97) = 0
    c: DistanceX(g96,g30) = 30
    c: DistanceX(g100,g51) = 30
    c: DistanceX(g26,g94) = 30
    c: DistanceX(g34,g88) = 30
    c: Coincident(g104,g107)
    c: Coincident(g106,g107)
    c: Coincident(g106,g105)
    c: Coincident(g104,g105)
    c: Coincident(g108,g109)
    c: Coincident(g108,g110)
    c: Coincident(g111,g110)
    c: Coincident(g111,g109)
    c: Parallel(g106,g104)
    c: Parallel(g104,g109)
    c: Parallel(g109,g110)
    c: Parallel(g110,g43)
    c: Parallel(g105,g107)
    c: Parallel(g107,g108)
    c: Parallel(g108,g111)
    c: Parallel(g111,g48)
    c: DistanceY(g108,g108) = 3
    c: Equal(g108,g107)
    c: DistanceX(g104,g104) = 30
    c: Equal(g104,g109)
    c: DistanceY(g39,g104) = 15
    c: DistanceY(g46,g109) = 15
    c: DistanceX(g40,g105) = 20
    c: DistanceX(g110,g45) = 20
    c: Coincident(g140,g139)
    c: Coincident(g139,g138)
    c: Coincident(g138,g137)
    c: Coincident(g137,g136)
    c: Coincident(g136,g135)
    c: Coincident(g135,g134)
    c: Coincident(g134,g133)
    c: Coincident(g132,g133)
    c: Coincident(g131,g130)
    c: Coincident(g129,g130)
    c: Coincident(g129,g128)
    c: Coincident(g128,g127)
    c: Coincident(g126,g127)
    c: Coincident(g126,g125)
    c: Coincident(g125,g124)
    c: Coincident(g124,g123)
    c: Coincident(g122,g123)
    c: Coincident(g121,g122)
    c: Coincident(g120,g121)
    c: Coincident(g119,g120)
    c: Coincident(g119,g118)
    c: Coincident(g117,g118)
    c: Coincident(g117,g116)
    c: Coincident(g115,g116)
    c: Coincident(g115,g114)
    c: Coincident(g113,g114)
    c: Coincident(g113,g112)
    c: Angle(g114) = 0
    c: Parallel(g114,g112)
    c: Parallel(g112,g116)
    c: Parallel(g116,g118)
    c: Parallel(g118,g120)
    c: Parallel(g120,g122)
    c: Parallel(g122,g124)
    c: Parallel(g124,g126)
    c: Parallel(g126,g128)
    c: Parallel(g128,g130)
    c: Parallel(g133,g135)
    c: Parallel(g135,g137)
    c: Parallel(g137,g139)
    c: Parallel(g140,g138)
    c: Parallel(g138,g136)
    c: Parallel(g136,g134)
    c: Parallel(g134,g132)
    c: Parallel(g131,g129)
    c: Parallel(g129,g127)
    c: Parallel(g127,g125)
    c: Parallel(g125,g123)
    c: Parallel(g123,g121)
    c: Parallel(g121,g119)
    c: Parallel(g119,g117)
    c: Parallel(g117,g115)
    c: Parallel(g115,g113)
    c: DistanceY(g113,g113) = 3
    c: DistanceY(g112,g115) = 0
    c: DistanceY(g117,g117) = 3
    c: DistanceY(g116,g119) = 0
    c: DistanceY(g132,g132) = 3
    c: DistanceY(g131,g131) = 3
    c: DistanceX(g135,g135) = 3
    c: DistanceX(g134,g137) = 0
    c: DistanceX(g139,g139) = 3
    c: DistanceX(g128,g128) = 3
    c: DistanceX(g125,g128) = 0
    c: DistanceX(g121,g124) = 0
    c: DistanceX(g124,g124) = 3
    c: DistanceX(g112,g112) = 20
    c: DistanceY(g120,g129) = 160
    c: DistanceY(g121,g121) = 40
    c: DistanceY(g123,g123) = 30
    c: Equal(g123,g125)
    c: Equal(g125,g127)
    c: Equal(g127,g136)
    c: Equal(g136,g138)
    c: Equal(g138,g140)
    c: DistanceX(g120,g120) = 37
    c: DistanceX(g118,g118) = 40
    c: Equal(g118,g116)
    c: Equal(g116,g114)
    c: DistanceX(g133,g133) = 20
    c: Coincident(g148,g147)
    c: Coincident(g146,g147)
    c: Coincident(g146,g145)
    c: Coincident(g148,g145)
    c: Coincident(g143,g142)
    c: Coincident(g143,g144)
    c: Coincident(g141,g144)
    c: Coincident(g141,g142)
    c: Parallel(g142,g144)
    c: Parallel(g144,g145)
    c: Parallel(g145,g147)
    c: Parallel(g147,g17)
    c: Parallel(g141,g143)
    c: Parallel(g143,g146)
    c: Parallel(g146,g148)
    c: Parallel(g148,g30)
    c: DistanceX(g142,g142) = 3
    c: DistanceX(g145,g145) = 3
    c: DistanceY(g141,g141) = 10
    c: DistanceY(g146,g146) = 10
    c: DistanceY(g142,g145) = 0
    c: DistanceX(g142,g145) = 110
    c: DistanceX(g145,g21) = 45
    c: DistanceY(g85,g146) = 10
    c: DistanceX(g130,g130) = 20
    c: Coincident(g153,g152)
    c: Coincident(g154,g153)
    c: Coincident(g154,g155)
    c: Coincident(g156,g155)
    c: Coincident(g156,g157)
    c: Coincident(g158,g157)
    c: Coincident(g158,g159)
    c: Coincident(g149,g159)
    c: Coincident(g150,g149)
    c: Coincident(g150,g151)
    c: Angle(g151) = 0
    c: Parallel(g151,g152)
    c: Parallel(g152,g154)
    c: Parallel(g154,g156)
    c: Parallel(g156,g158)
    c: Parallel(g158,g149)
    c: Parallel(g157,g155)
    c: Parallel(g155,g153)
    c: Parallel(g150,g159)
    c: DistanceX(g151,g151) = 22
    c: DistanceX(g153,g149) = 0
    c: DistanceX(g149,g149) = 20
    c: DistanceX(g155,g158) = 0
    c: DistanceX(g156,g156) = 3
    c: DistanceY(g150,g150) = 3
    c: DistanceY(g153,g153) = 3
    c: DistanceY(g149,g153) = 30
    c: DistanceY(g157,g157) = 10
    c: DistanceY(g159,g159) = 10
    c: Coincident(g187,g164)
    c: Coincident(g164,g163)
    c: Coincident(g163,g162)
    c: Coincident(g160,g162)
    c: Coincident(g161,g160)
    c: Coincident(g161,g165)
    c: Coincident(g166,g165)
    c: Coincident(g166,g167)
    c: Coincident(g167,g168)
    c: Coincident(g169,g168)
    c: Coincident(g186,g187)
    c: Coincident(g186,g185)
    c: Coincident(g184,g185)
    c: Coincident(g184,g183)
    c: Coincident(g182,g183)
    c: Coincident(g182,g181)
    c: Coincident(g170,g171)
    c: Coincident(g170,g169)
    c: Coincident(g172,g171)
    c: Coincident(g180,g181)
    c: Coincident(g180,g179)
    c: Coincident(g178,g179)
    c: Coincident(g178,g177)
    c: Coincident(g177,g176)
    c: Coincident(g175,g176)
    c: Coincident(g175,g174)
    c: Coincident(g173,g174)
    c: Coincident(g172,g173)
    c: Angle(g162) = -3.14159
    c: Perpendicular(g165,g162)
    c: Parallel(g162,g161)
    c: Parallel(g161,g164)
    c: Parallel(g164,g186)
    c: Parallel(g186,g166)
    c: Parallel(g166,g168)
    c: Parallel(g168,g184)
    c: Parallel(g184,g182)
    c: Parallel(g182,g170)
    c: Parallel(g170,g172)
    c: Parallel(g172,g180)
    c: Parallel(g180,g178)
    c: Parallel(g178,g176)
    c: Parallel(g176,g174)
    c: Parallel(g163,g160)
    c: Parallel(g160,g165)
    c: Parallel(g165,g187)
    c: Parallel(g187,g185)
    c: Parallel(g185,g167)
    c: Parallel(g167,g169)
    c: Parallel(g169,g183)
    c: Parallel(g183,g181)
    c: Parallel(g181,g171)
    c: Parallel(g171,g173)
    c: Parallel(g173,g175)
    c: Parallel(g175,g177)
    c: Parallel(g177,g179)
    c: DistanceY(g160,g160) = 3
    c: DistanceX(g166,g166) = 3
    c: DistanceX(g186,g186) = 3
    c: DistanceX(g182,g182) = 3
    c: DistanceX(g170,g170) = 3
    c: DistanceX(g184,g181) = 0
    c: DistanceX(g167,g170) = 0
    c: DistanceX(g169,g172) = 0
    c: DistanceX(g179,g182) = 0
    c: DistanceX(g162,g162) = 30
    c: DistanceX(g161,g161) = 3
    c: DistanceX(g164,g164) = 3
    c: DistanceX(g176,g176) = 10
    c: DistanceY(g165,g165) = 40
    c: DistanceY(g167,g167) = 30
    c: Equal(g165,g187)
    c: Equal(g167,g169)
    c: Equal(g169,g171)
    c: Equal(g171,g181)
    c: Equal(g181,g183)
    c: Equal(g183,g185)
    c: DistanceX(g174,g174) = 13
    c: Coincident(g191,g192)
    c: Coincident(g193,g192)
    c: Coincident(g194,g193)
    c: Coincident(g191,g190)
    c: Coincident(g190,g189)
    c: Coincident(g189,g188)
    c: Parallel(g191,g189)
    c: Parallel(g189,g193)
    c: Parallel(g194,g188)
    c: Parallel(g188,g192)
    c: Parallel(g192,g190)
    c: DistanceY(g192,g189) = 0
    c: DistanceY(g192,g192) = 3
    c: DistanceX(g191,g191) = 10
    c: DistanceX(g189,g189) = 10
    c: DistanceX(g194,g188) = 30
    c: DistanceY(g188,g188) = 157
    c: DistanceY(g173,g173) = 30
    c: Equal(g173,g179)
    c: DistanceY(g177,g177) = 3
    c: DistanceY(g177,g174) = 0
    c: Coincident(g196,g195)
    c: Coincident(g195,g203)
    c: Coincident(g204,g203)
    c: Coincident(g205,g204)
    c: Coincident(g205,g206)
    c: Coincident(g206,g207)
    c: Coincident(g207,g208)
    c: Coincident(g209,g208)
    c: Coincident(g209,g210)
    c: Coincident(g211,g210)
    c: Coincident(g211,g212)
    c: Coincident(g220,g221)
    c: Coincident(g218,g219)
    c: Coincident(g217,g218)
    c: Coincident(g216,g217)
    c: Coincident(g215,g216)
    c: Coincident(g214,g215)
    c: Coincident(g214,g213)
    c: Coincident(g202,g213)
    c: Coincident(g200,g201)
    c: Coincident(g199,g200)
    c: Coincident(g199,g198)
    c: Coincident(g197,g198)
    c: Coincident(g197,g196)
    c: Angle(g196) = 3.14159
    c: Perpendicular(g204,g196)
    c: Parallel(g196,g203)
    c: Parallel(g203,g198)
    c: Parallel(g198,g200)
    c: Parallel(g214,g216)
    c: Parallel(g216,g218)
    c: Parallel(g211,g209)
    c: Parallel(g209,g207)
    c: Parallel(g207,g205)
    c: Parallel(g204,g206)
    c: Parallel(g206,g208)
    c: Parallel(g208,g210)
    c: Parallel(g210,g212)
    c: Parallel(g212,g221)
    c: Parallel(g219,g217)
    c: Parallel(g217,g215)
    c: Parallel(g215,g213)
    c: Parallel(g201,g199)
    c: Parallel(g199,g197)
    c: Parallel(g197,g195)
    c: DistanceY(g197,g195) = 0
    c: DistanceY(g198,g201) = 0
    c: DistanceY(g195,g195) = 3
    c: DistanceY(g199,g199) = 3
    c: DistanceX(g207,g204) = 0
    c: DistanceX(g211,g208) = 0
    c: DistanceX(g207,g207) = 3
    c: DistanceX(g209,g209) = 3
    c: DistanceX(g215,g218) = 0
    c: DistanceX(g216,g216) = 3
    c: DistanceX(g214,g214) = 3
    c: DistanceY(g220,g227) = 27
    c: DistanceY(g227,g221) = 0
    c: DistanceX(g220,g220) = 110
    c: DistanceX(g217,g220) = 45
    c: DistanceX(g220,g210) = 45
    c: DistanceX(g200,g200) = 40
    c: DistanceX(g196,g196) = 40
    c: DistanceX(g198,g198) = 20
    c: DistanceY(g204,g204) = 40
    c: DistanceY(g206,g206) = 30
    c: Equal(g206,g208)
    c: Equal(g208,g210)
    c: Equal(g210,g213)
    c: Equal(g213,g215)
    c: Equal(g215,g217)
    c: DistanceY(g212,g212) = 30
    c: Radius(g222) = 10
    c: DistanceX(g140,g222) = 31
    c: DistanceY(g113,g222) = 25
    c: Radius(g223) = 1.6
    c: Radius(g224) = 1.6
    c: DistanceX(g4,g223) = 4
    c: DistanceY(g223,g4) = 4.6
    c: DistanceX(g224,g7) = 4
    c: DistanceY(g224,g7) = 4.6
    c: Coincident(g229,g230)
    c: Coincident(g229,g228)
    c: DistanceY(g218,g220) = 0
    c: Coincident(g221,g230)
    c: Coincident(g228,g212)
    c: DistanceY(g228,g212) = 0
    c: DistanceY(g229,g221) = 0
    c: DistanceX(g229,g228) = 0
    c: DistanceX(g228,g228) = 20
    c: Coincident(g219,g225)
    c: DistanceY(g219,g225) = 0
    c: Coincident(g225,g226)
    c: DistanceX(g225,g226) = 0
    c: Coincident(g226,g227)
    c: DistanceY(g227,g226) = 0
    c: DistanceY(g219,g219) = 30
    c: Radius(g231) = 1.6
    c: Equal(g231,g232)
    c: Equal(g232,g233)
    c: Equal(g233,g234)
    c: DistanceY(g231,g232) = 0
    c: DistanceX(g231,g232) = 17.9
    c: DistanceY(g233,g234) = 0
    c: DistanceX(g233,g234) = 17.9
    c: DistanceY(g232,g233) = 0
    c: DistanceX(g232,g233) = 93
    c: DistanceY(g201,g232) = 25
    c: DistanceX(g202,g231) = 35.6
    c: Parallel(g207,g196)
    c: Coincident(g240,g241)
    c: Coincident(g241,g242)
    c: Coincident(g242,g235)
    c: Coincident(g236,g235)
    c: Coincident(g236,g237)
    c: Coincident(g238,g237)
    c: Coincident(g239,g238)
    c: Coincident(g240,g239)
    c: Coincident(g245,g244)
    c: Coincident(g246,g245)
    c: Coincident(g246,g247)
    c: Coincident(g248,g247)
    c: Angle(g240) = 3.14159
    c: Angle(g246) = 3.14159
    c: Perpendicular(g239,g240)
    c: Perpendicular(g245,g246)
    c: Parallel(g246,g244)
    c: Parallel(g244,g243)
    c: Parallel(g243,g248)
    c: Parallel(g240,g242)
    c: Parallel(g242,g236)
    c: Parallel(g236,g238)
    c: Parallel(g239,g237)
    c: Parallel(g237,g235)
    c: Parallel(g235,g241)
    c: DistanceY(g235,g237) = 0
    c: DistanceY(g244,g247) = 0
    c: DistanceY(g245,g245) = 3
    c: DistanceY(g237,g237) = 3
    c: DistanceX(g240,g240) = 109
    c: DistanceX(g243,g243) = 109
    c: DistanceX(g248,g248) = 30
    c: DistanceX(g244,g244) = 30
    c: DistanceX(g242,g242) = 30
    c: DistanceX(g238,g238) = 30
    c: DistanceY(g241,g241) = 33
    c: DistanceY(g248,g243) = 30
    c: DistanceX(g225,g225) = 20
    c: Parallel(g250,g200)
    c: Parallel(g249,g213)
    c: DistanceX(g250,g250) = 23
    c: DistanceY(g249,g249) = 40
    c: Coincident(g201,g250)
    c: Parallel(g201,g213)
    c: Coincident(g250,g249)
    c: Parallel(g202,g250)
    c: Coincident(g249,g202)
    c: DistanceX(g202,g202) = 27
    c: Parallel(g220,g196)
    c: Radius(g251) = 1.6
    c: Equal(g251,g252)
    c: DistanceY(g251,g252) = 0
    c: DistanceX(g251,g252) = 17.9
    c: DistanceX(g220,g251) = 46.05
    c: DistanceY(g251,g220) = 12
    c: Coincident(g254,g253)
    c: Coincident(g255,g254)
    c: Coincident(g255,g256)
    c: Coincident(g256,g257)
    c: Coincident(g194,g253)
    c: Coincident(g188,g257)
    c: Parallel(g256,g254)
    c: Parallel(g254,g188)
    c: Parallel(g253,g255)
    c: Parallel(g255,g257)
    c: Parallel(g257,g191)
    c: DistanceX(g255,g255) = 10
    c: DistanceX(g257,g257) = 10
    c: Angle(g191) = -3.14159
    c: Perpendicular(g192,g191)
    c: Perpendicular(g150,g151)
    c: Coincident(g261,g262)
    c: Coincident(g260,g261)
    c: Coincident(g260,g259)
    c: Coincident(g259,g258)
    c: Coincident(g152,g258)
    c: Coincident(g151,g262)
    c: Parallel(g262,g260)
    c: Parallel(g260,g258)
    c: Parallel(g258,g150)
    c: Parallel(g261,g259)
    c: Parallel(g259,g151)
    c: DistanceX(g261,g258) = 0
    c: DistanceX(g261,g261) = 3
    c: DistanceY(g260,g260) = 10
    c: DistanceY(g262,g262) = 13
    c: DistanceY(g254,g254) = 3
    c: Coincident(g132,g263)
    c: Coincident(g131,g263)
    c: Parallel(g263,g130)
    c: DistanceX(g263,g263) = 154
    c: Coincident(g264,g265)
    c: DistanceX(g264,g264) = 20
    c: Perpendicular(g264,g265)
    c: Parallel(g264,g116)
    c: DistanceY(g265,g265) = 40
    c: Coincident(g140,g264)
    c: Coincident(g112,g265)
    c: Parallel(g140,g265)
    c: Parallel(g139,g264)
    c: Radius(g266) = 1.6
    c: Equal(g266,g267)
    c: DistanceY(g266,g267) = 0
    c: DistanceX(g266,g267) = 17.9
    c: DistanceX(g243,g266) = 45.55
    c: DistanceY(g266,g243) = 10
    c: Parallel(g268,g248)
    c: DistanceX(g269,g268) = 0
    c: Coincident(g244,g268)
    c: Coincident(g243,g269)
    c: Coincident(g271,g270)
    c: Perpendicular(g270,g271)
    c: Parallel(g271,g196)
    c: Parallel(g214,g196)
    c: DistanceY(g270,g270) = 5
    c: DistanceX(g271,g271) = 4
    c: Coincident(g227,g270)
    c: DistanceX(g227,g227) = 18
    c: Coincident(g271,g272)
    c: Coincident(g220,g272)
    c: Coincident(g274,g273)
    c: Coincident(g275,g274)
    c: Coincident(g276,g275)
    c: Coincident(g277,g276)
    c: Coincident(g278,g277)
    c: Coincident(g278,g279)
    c: Coincident(g280,g279)
    c: Coincident(g280,g281)
    c: Coincident(g282,g281)
    c: Coincident(g282,g283)
    c: Coincident(g284,g283)
    c: Coincident(g285,g284)
    c: Coincident(g285,g286)
    c: Coincident(g287,g286)
    c: Coincident(g288,g287)
    c: Coincident(g288,g289)
    c: Coincident(g273,g290)
    c: Coincident(g289,g290)
    c: Angle(g286) = -3.14159
    c: Perpendicular(g285,g286)
    c: Parallel(g286,g288)
    c: Parallel(g288,g290)
    c: Parallel(g290,g274)
    c: Parallel(g274,g276)
    c: Parallel(g276,g278)
    c: Parallel(g278,g280)
    c: Parallel(g280,g282)
    c: Parallel(g282,g284)
    c: Parallel(g285,g287)
    c: Parallel(g287,g289)
    c: Parallel(g289,g273)
    c: Parallel(g273,g275)
    c: Parallel(g275,g277)
    c: Parallel(g277,g279)
    c: Parallel(g279,g281)
    c: Parallel(g281,g283)
    c: DistanceY(g287,g276) = 30
    c: DistanceY(g273,g273) = 10
    c: DistanceY(g289,g289) = 10
    c: DistanceY(g277,g277) = 3
    c: DistanceX(g274,g274) = 3
    c: DistanceX(g274,g289) = 0
    c: DistanceX(g276,g276) = 20
    c: DistanceY(g285,g285) = 3
    c: DistanceY(g287,g284) = 0
    c: DistanceX(g284,g284) = 6
    c: DistanceX(g282,g282) = 3
    c: DistanceX(g282,g279) = 0
    c: DistanceX(g287,g276) = 0
    c: DistanceX(g278,g278) = 22
    c: DistanceY(g281,g281) = 10
    c: DistanceY(g283,g283) = 10
    c: Parallel(g247,g245)
    c: Coincident(g269,g268)
    c: Coincident(g248,g291)
FEATURE [App::Part] Part001
  Origin = -> Origin001
FEATURE [Sketcher::SketchObject] Sketch001
  sketch-geometry (192):
    g0: LineSegment StartX=-726.643 StartY=372.942 StartZ=0 EndX=-726.643 EndY=345.942 EndZ=0
    g1: LineSegment StartX=-726.643 StartY=345.942 StartZ=0 EndX=-729.643 EndY=345.942 EndZ=0
    g2: LineSegment StartX=-729.643 StartY=345.942 StartZ=0 EndX=-729.643 EndY=315.942 EndZ=0
    g3: LineSegment StartX=-729.643 StartY=315.942 StartZ=0 EndX=-726.643 EndY=315.942 EndZ=0
    g4: LineSegment StartX=-726.643 StartY=315.942 StartZ=0 EndX=-726.643 EndY=293.942 EndZ=0
    g5: LineSegment StartX=-726.643 StartY=293.942 StartZ=0 EndX=-729.643 EndY=293.942 EndZ=0
    g6: LineSegment StartX=-729.643 StartY=293.942 StartZ=0 EndX=-729.643 EndY=263.942 EndZ=0
    g7: LineSegment StartX=-729.643 StartY=263.942 StartZ=0 EndX=-726.643 EndY=263.942 EndZ=0
    g8: LineSegment StartX=-726.643 StartY=263.942 StartZ=0 EndX=-726.643 EndY=230.842 EndZ=0
    g9: LineSegment StartX=-726.643 StartY=372.942 StartZ=0 EndX=-677.643 EndY=372.942 EndZ=0
    g10: LineSegment StartX=-677.643 StartY=372.942 StartZ=0 EndX=-677.643 EndY=345.942 EndZ=0
    g11: LineSegment StartX=-677.643 StartY=345.942 StartZ=0 EndX=-674.643 EndY=345.942 EndZ=0
    g12: LineSegment StartX=-674.643 StartY=345.942 StartZ=0 EndX=-674.643 EndY=315.942 EndZ=0
    g13: LineSegment StartX=-674.643 StartY=315.942 StartZ=0 EndX=-677.643 EndY=315.942 EndZ=0
    g14: LineSegment StartX=-677.643 StartY=315.942 StartZ=0 EndX=-677.643 EndY=293.942 EndZ=0
    g15: LineSegment StartX=-677.643 StartY=293.942 StartZ=0 EndX=-674.643 EndY=293.942 EndZ=0
    g16: LineSegment StartX=-674.643 StartY=293.942 StartZ=0 EndX=-674.643 EndY=263.942 EndZ=0
    g17: LineSegment StartX=-674.643 StartY=263.942 StartZ=0 EndX=-677.643 EndY=263.942 EndZ=0
    g18: LineSegment StartX=-677.643 StartY=263.942 StartZ=0 EndX=-677.643 EndY=230.842 EndZ=0
    g19: LineSegment StartX=-726.643 StartY=230.842 StartZ=0 EndX=-723.643 EndY=230.842 EndZ=0
    g20: LineSegment StartX=-723.643 StartY=230.842 StartZ=0 EndX=-723.643 EndY=233.842 EndZ=0
    g21: LineSegment StartX=-723.643 StartY=233.842 StartZ=0 EndX=-680.643 EndY=233.842 EndZ=0
    g22: LineSegment StartX=-680.643 StartY=233.842 StartZ=0 EndX=-680.643 EndY=230.842 EndZ=0
    g23: LineSegment StartX=-680.643 StartY=230.842 StartZ=0 EndX=-677.643 EndY=230.842 EndZ=0
    g24: LineSegment StartX=-602.423 StartY=372.488 StartZ=0 EndX=-553.423 EndY=372.488 EndZ=0
    g25: LineSegment StartX=-602.423 StartY=372.488 StartZ=0 EndX=-602.423 EndY=345.488 EndZ=0
    g26: LineSegment StartX=-602.423 StartY=345.488 StartZ=0 EndX=-605.423 EndY=345.488 EndZ=0
    g27: LineSegment StartX=-605.423 StartY=345.488 StartZ=0 EndX=-605.423 EndY=315.488 EndZ=0
    g28: LineSegment StartX=-605.423 StartY=315.488 StartZ=0 EndX=-602.423 EndY=315.488 EndZ=0
    g29: LineSegment StartX=-602.423 StartY=315.488 StartZ=0 EndX=-602.423 EndY=293.488 EndZ=0
    g30: LineSegment StartX=-602.423 StartY=293.488 StartZ=0 EndX=-605.423 EndY=293.488 EndZ=0
    g31: LineSegment StartX=-605.423 StartY=293.488 StartZ=0 EndX=-605.423 EndY=263.488 EndZ=0
    g32: LineSegment StartX=-605.423 StartY=263.488 StartZ=0 EndX=-602.423 EndY=263.488 EndZ=0
    g33: LineSegment StartX=-602.423 StartY=263.488 StartZ=0 EndX=-602.423 EndY=230.388 EndZ=0
    g34: LineSegment StartX=-602.423 StartY=230.388 StartZ=0 EndX=-599.423 EndY=230.388 EndZ=0
    g35: LineSegment StartX=-599.423 StartY=230.388 StartZ=0 EndX=-599.423 EndY=233.388 EndZ=0
    g36: LineSegment StartX=-599.423 StartY=233.388 StartZ=0 EndX=-556.423 EndY=233.388 EndZ=0
    g37: LineSegment StartX=-556.423 StartY=233.388 StartZ=0 EndX=-556.423 EndY=230.388 EndZ=0
    g38: LineSegment StartX=-556.423 StartY=230.388 StartZ=0 EndX=-553.423 EndY=230.388 EndZ=0
    g39: LineSegment StartX=-553.423 StartY=230.388 StartZ=0 EndX=-553.423 EndY=263.488 EndZ=0
    g40: LineSegment StartX=-553.423 StartY=263.488 StartZ=0 EndX=-550.423 EndY=263.488 EndZ=0
    g41: LineSegment StartX=-550.423 StartY=263.488 StartZ=0 EndX=-550.423 EndY=293.488 EndZ=0
    g42: LineSegment StartX=-550.423 StartY=293.488 StartZ=0 EndX=-553.423 EndY=293.488 EndZ=0
    g43: LineSegment StartX=-553.423 StartY=293.488 StartZ=0 EndX=-553.423 EndY=315.488 EndZ=0
    g44: LineSegment StartX=-553.423 StartY=315.488 StartZ=0 EndX=-550.423 EndY=315.488 EndZ=0
    g45: LineSegment StartX=-550.423 StartY=315.488 StartZ=0 EndX=-550.423 EndY=345.488 EndZ=0
    g46: LineSegment StartX=-550.423 StartY=345.488 StartZ=0 EndX=-553.423 EndY=345.488 EndZ=0
    g47: LineSegment StartX=-553.423 StartY=345.488 StartZ=0 EndX=-553.423 EndY=372.488 EndZ=0
    g48: LineSegment StartX=-561.423 StartY=357.488 StartZ=0 EndX=-558.423 EndY=357.488 EndZ=0
    g49: LineSegment StartX=-558.423 StartY=357.488 StartZ=0 EndX=-558.423 EndY=245.388 EndZ=0
    g50: LineSegment StartX=-558.423 StartY=245.388 StartZ=0 EndX=-561.423 EndY=245.388 EndZ=0
    g51: LineSegment StartX=-561.423 StartY=245.388 StartZ=0 EndX=-561.423 EndY=357.488 EndZ=0
    g52: LineSegment StartX=-592.423 StartY=245.388 StartZ=0 EndX=-572.423 EndY=245.388 EndZ=0
    g53: LineSegment StartX=-592.423 StartY=245.388 StartZ=0 EndX=-592.423 EndY=242.388 EndZ=0
    g54: LineSegment StartX=-592.423 StartY=242.388 StartZ=0 EndX=-572.423 EndY=242.388 EndZ=0
    g55: LineSegment StartX=-572.423 StartY=245.388 StartZ=0 EndX=-572.423 EndY=242.388 EndZ=0
    g56: LineSegment StartX=-656.028 StartY=373.881 StartZ=0 EndX=-626.028 EndY=373.881 EndZ=0
    g57: LineSegment StartX=-656.028 StartY=373.881 StartZ=0 EndX=-656.028 EndY=346.881 EndZ=0
    g58: LineSegment StartX=-656.028 StartY=346.881 StartZ=0 EndX=-653.028 EndY=346.881 EndZ=0
    g59: LineSegment StartX=-626.028 StartY=373.881 StartZ=0 EndX=-626.028 EndY=346.881 EndZ=0
    g60: LineSegment StartX=-626.028 StartY=346.881 StartZ=0 EndX=-629.028 EndY=346.881 EndZ=0
    g61: LineSegment StartX=-653.028 StartY=346.881 StartZ=0 EndX=-653.028 EndY=316.881 EndZ=0
    g62: LineSegment StartX=-629.028 StartY=346.881 StartZ=0 EndX=-629.028 EndY=316.881 EndZ=0
    g63: LineSegment StartX=-653.028 StartY=316.881 StartZ=0 EndX=-656.028 EndY=316.881 EndZ=0
    g64: LineSegment StartX=-629.028 StartY=316.881 StartZ=0 EndX=-626.028 EndY=316.881 EndZ=0
    g65: LineSegment StartX=-656.028 StartY=316.881 StartZ=0 EndX=-656.028 EndY=294.881 EndZ=0
    g66: LineSegment StartX=-656.028 StartY=294.881 StartZ=0 EndX=-653.028 EndY=294.881 EndZ=0
    g67: LineSegment StartX=-626.028 StartY=316.881 StartZ=0 EndX=-626.028 EndY=294.881 EndZ=0
    g68: LineSegment StartX=-626.028 StartY=294.881 StartZ=0 EndX=-629.028 EndY=294.881 EndZ=0
    g69: LineSegment StartX=-653.028 StartY=294.881 StartZ=0 EndX=-653.028 EndY=264.881 EndZ=0
    g70: LineSegment StartX=-653.028 StartY=264.881 StartZ=0 EndX=-656.028 EndY=264.881 EndZ=0
    g71: LineSegment StartX=-656.028 StartY=264.881 StartZ=0 EndX=-656.028 EndY=231.781 EndZ=0
    g72: LineSegment StartX=-656.028 StartY=231.781 StartZ=0 EndX=-626.028 EndY=231.781 EndZ=0
    g73: LineSegment StartX=-629.028 StartY=294.881 StartZ=0 EndX=-629.028 EndY=264.881 EndZ=0
    g74: LineSegment StartX=-629.028 StartY=264.881 StartZ=0 EndX=-626.028 EndY=264.881 EndZ=0
    g75: LineSegment StartX=-626.028 StartY=264.881 StartZ=0 EndX=-626.028 EndY=231.781 EndZ=0
    g76: LineSegment StartX=-713.87 StartY=156.063 StartZ=0 EndX=-683.87 EndY=156.063 EndZ=0
    g77: LineSegment StartX=-683.87 StartY=156.063 StartZ=0 EndX=-683.87 EndY=153.063 EndZ=0
    g78: LineSegment StartX=-683.87 StartY=153.063 StartZ=0 EndX=-653.87 EndY=153.063 EndZ=0
    g79: LineSegment StartX=-653.87 StartY=153.063 StartZ=0 EndX=-653.87 EndY=156.063 EndZ=0
    g80: LineSegment StartX=-653.87 StartY=156.063 StartZ=0 EndX=-633.87 EndY=156.063 EndZ=0
    g81: LineSegment StartX=-633.87 StartY=156.063 StartZ=0 EndX=-633.87 EndY=153.063 EndZ=0
    g82: LineSegment StartX=-633.87 StartY=153.063 StartZ=0 EndX=-603.87 EndY=153.063 EndZ=0
    g83: LineSegment StartX=-603.87 StartY=153.063 StartZ=0 EndX=-603.87 EndY=156.063 EndZ=0
    g84: LineSegment StartX=-603.87 StartY=156.063 StartZ=0 EndX=-573.87 EndY=156.063 EndZ=0
    g85: LineSegment StartX=-573.87 StartY=156.063 StartZ=0 EndX=-573.87 EndY=166.063 EndZ=0
    g86: LineSegment StartX=-573.87 StartY=166.063 StartZ=0 EndX=-570.87 EndY=166.063 EndZ=0
    g87: LineSegment StartX=-570.87 StartY=166.063 StartZ=0 EndX=-570.87 EndY=186.063 EndZ=0
    g88: LineSegment StartX=-570.87 StartY=186.063 StartZ=0 EndX=-573.87 EndY=186.063 EndZ=0
    g89: LineSegment StartX=-573.87 StartY=186.063 StartZ=0 EndX=-573.87 EndY=205.063 EndZ=0
    g90: LineSegment StartX=-573.87 StartY=205.063 StartZ=0 EndX=-603.87 EndY=205.063 EndZ=0
    g91: LineSegment StartX=-603.87 StartY=205.063 StartZ=0 EndX=-603.87 EndY=208.063 EndZ=0
    g92: LineSegment StartX=-603.87 StartY=208.063 StartZ=0 EndX=-633.87 EndY=208.063 EndZ=0
    g93: LineSegment StartX=-633.87 StartY=208.063 StartZ=0 EndX=-633.87 EndY=205.063 EndZ=0
    g94: LineSegment StartX=-633.87 StartY=205.063 StartZ=0 EndX=-653.87 EndY=205.063 EndZ=0
    g95: LineSegment StartX=-653.87 StartY=205.063 StartZ=0 EndX=-653.87 EndY=208.063 EndZ=0
    g96: LineSegment StartX=-653.87 StartY=208.063 StartZ=0 EndX=-683.87 EndY=208.063 EndZ=0
    g97: LineSegment StartX=-683.87 StartY=208.063 StartZ=0 EndX=-683.87 EndY=205.063 EndZ=0
    g98: LineSegment StartX=-683.87 StartY=205.063 StartZ=0 EndX=-713.87 EndY=205.063 EndZ=0
    g99: LineSegment StartX=-713.87 StartY=205.063 StartZ=0 EndX=-713.87 EndY=186.063 EndZ=0
    g100: LineSegment StartX=-713.87 StartY=186.063 StartZ=0 EndX=-716.87 EndY=186.063 EndZ=0
    g101: LineSegment StartX=-716.87 StartY=186.063 StartZ=0 EndX=-716.87 EndY=166.063 EndZ=0
    g102: LineSegment StartX=-716.87 StartY=166.063 StartZ=0 EndX=-713.87 EndY=166.063 EndZ=0
    g103: LineSegment StartX=-713.87 StartY=166.063 StartZ=0 EndX=-713.87 EndY=156.063 EndZ=0
    g104: LineSegment StartX=-742.656 StartY=25.9999 StartZ=0 EndX=-718.656 EndY=25.9999 EndZ=0
    g105: LineSegment StartX=-705.656 StartY=25.9999 StartZ=0 EndX=-705.656 EndY=22.9999 EndZ=0
    g106: LineSegment StartX=-705.656 StartY=22.9999 StartZ=0 EndX=-665.656 EndY=22.9999 EndZ=0
    g107: LineSegment StartX=-665.656 StartY=22.9999 StartZ=0 EndX=-665.656 EndY=25.9999 EndZ=0
    g108: LineSegment StartX=-665.656 StartY=25.9999 StartZ=0 EndX=-625.656 EndY=25.9999 EndZ=0
    g109: LineSegment StartX=-625.656 StartY=25.9999 StartZ=0 EndX=-625.656 EndY=22.9999 EndZ=0
    g110: LineSegment StartX=-625.656 StartY=22.9999 StartZ=0 EndX=-585.656 EndY=22.9999 EndZ=0
    g111: LineSegment StartX=-585.656 StartY=22.9999 StartZ=0 EndX=-585.656 EndY=25.9999 EndZ=0
    g112: LineSegment StartX=-572.656 StartY=25.9999 StartZ=0 EndX=-548.656 EndY=25.9999 EndZ=0
    g113: LineSegment StartX=-548.656 StartY=25.9999 StartZ=0 EndX=-548.656 EndY=28.9999 EndZ=0
    g114: LineSegment StartX=-548.656 StartY=28.9999 StartZ=0 EndX=-545.656 EndY=28.9999 EndZ=0
    g115: LineSegment StartX=-545.656 StartY=28.9999 StartZ=0 EndX=-545.656 EndY=71.9999 EndZ=0
    g116: LineSegment StartX=-545.656 StartY=71.9999 StartZ=0 EndX=-548.656 EndY=71.9999 EndZ=0
    g117: LineSegment StartX=-548.656 StartY=71.9999 StartZ=0 EndX=-548.656 EndY=74.9999 EndZ=0
    g118: LineSegment StartX=-548.656 StartY=74.9999 StartZ=0 EndX=-572.656 EndY=74.9999 EndZ=0
    g119: LineSegment StartX=-575.656 StartY=25.9999 StartZ=0 EndX=-575.656 EndY=28.9999 EndZ=0
    g120: LineSegment StartX=-575.656 StartY=28.9999 StartZ=0 EndX=-572.656 EndY=28.9999 EndZ=0
    g121: LineSegment StartX=-572.656 StartY=28.9999 StartZ=0 EndX=-572.656 EndY=25.9999 EndZ=0
    g122: LineSegment StartX=-572.656 StartY=74.9999 StartZ=0 EndX=-572.656 EndY=71.9999 EndZ=0
    g123: LineSegment StartX=-572.656 StartY=71.9999 StartZ=0 EndX=-575.656 EndY=71.9999 EndZ=0
    g124: LineSegment StartX=-575.656 StartY=71.9999 StartZ=0 EndX=-575.656 EndY=74.9999 EndZ=0
    g125: LineSegment StartX=-575.656 StartY=74.9999 StartZ=0 EndX=-605.656 EndY=74.9999 EndZ=0
    g126: LineSegment StartX=-605.656 StartY=74.9999 StartZ=0 EndX=-605.656 EndY=77.9999 EndZ=0
    g127: LineSegment StartX=-605.656 StartY=77.9999 StartZ=0 EndX=-635.656 EndY=77.9999 EndZ=0
    g128: LineSegment StartX=-635.656 StartY=77.9999 StartZ=0 EndX=-635.656 EndY=74.9999 EndZ=0
    g129: LineSegment StartX=-635.656 StartY=74.9999 StartZ=0 EndX=-655.656 EndY=74.9999 EndZ=0
    g130: LineSegment StartX=-655.656 StartY=74.9999 StartZ=0 EndX=-655.656 EndY=77.9999 EndZ=0
    g131: LineSegment StartX=-655.656 StartY=77.9999 StartZ=0 EndX=-685.656 EndY=77.9999 EndZ=0
    g132: LineSegment StartX=-685.656 StartY=77.9999 StartZ=0 EndX=-685.656 EndY=74.9999 EndZ=0
    g133: LineSegment StartX=-685.656 StartY=74.9999 StartZ=0 EndX=-715.656 EndY=74.9999 EndZ=0
    g134: LineSegment StartX=-715.656 StartY=74.9999 StartZ=0 EndX=-715.656 EndY=71.9999 EndZ=0
    g135: LineSegment StartX=-715.656 StartY=71.9999 StartZ=0 EndX=-718.656 EndY=71.9999 EndZ=0
    g136: LineSegment StartX=-718.656 StartY=71.9999 StartZ=0 EndX=-718.656 EndY=74.9999 EndZ=0
    g137: LineSegment StartX=-718.656 StartY=74.9999 StartZ=0 EndX=-742.656 EndY=74.9999 EndZ=0
    g138: LineSegment StartX=-742.656 StartY=74.9999 StartZ=0 EndX=-742.656 EndY=71.9999 EndZ=0
    g139: LineSegment StartX=-742.656 StartY=71.9999 StartZ=0 EndX=-745.656 EndY=71.9999 EndZ=0
    g140: LineSegment StartX=-745.656 StartY=71.9999 StartZ=0 EndX=-745.656 EndY=28.9999 EndZ=0
    g141: LineSegment StartX=-745.656 StartY=28.9999 StartZ=0 EndX=-742.656 EndY=28.9999 EndZ=0
    g142: LineSegment StartX=-742.656 StartY=28.9999 StartZ=0 EndX=-742.656 EndY=25.9999 EndZ=0
    g143: LineSegment StartX=-718.656 StartY=25.9999 StartZ=0 EndX=-718.656 EndY=28.9999 EndZ=0
    g144: LineSegment StartX=-718.656 StartY=28.9999 StartZ=0 EndX=-715.656 EndY=28.9999 EndZ=0
    g145: LineSegment StartX=-715.656 StartY=28.9999 StartZ=0 EndX=-715.656 EndY=25.9999 EndZ=0
    g146: LineSegment StartX=-715.656 StartY=25.9999 StartZ=0 EndX=-705.656 EndY=25.9999 EndZ=0
    g147: LineSegment StartX=-585.656 StartY=25.9999 StartZ=0 EndX=-575.656 EndY=25.9999 EndZ=0
    g148: LineSegment StartX=-720.709 StartY=131.573 StartZ=0 EndX=-720.709 EndY=116.573 EndZ=0
    g149: LineSegment StartX=-720.709 StartY=131.573 StartZ=0 EndX=-690.709 EndY=131.573 EndZ=0
    g150: LineSegment StartX=-690.709 StartY=131.573 StartZ=0 EndX=-690.709 EndY=128.573 EndZ=0
    g151: LineSegment StartX=-690.709 StartY=128.573 StartZ=0 EndX=-660.709 EndY=128.573 EndZ=0
    g152: LineSegment StartX=-660.709 StartY=128.573 StartZ=0 EndX=-660.709 EndY=131.573 EndZ=0
    g153: LineSegment StartX=-660.709 StartY=131.573 StartZ=0 EndX=-640.709 EndY=131.573 EndZ=0
    g154: LineSegment StartX=-640.709 StartY=131.573 StartZ=0 EndX=-640.709 EndY=128.573 EndZ=0
    g155: LineSegment StartX=-640.709 StartY=128.573 StartZ=0 EndX=-610.709 EndY=128.573 EndZ=0
    g156: LineSegment StartX=-610.709 StartY=128.573 StartZ=0 EndX=-610.709 EndY=131.573 EndZ=0
    g157: LineSegment StartX=-610.709 StartY=131.573 StartZ=0 EndX=-580.709 EndY=131.573 EndZ=0
    g158: LineSegment StartX=-580.709 StartY=131.573 StartZ=0 EndX=-580.709 EndY=116.573 EndZ=0
    g159: LineSegment StartX=-580.709 StartY=116.573 StartZ=0 EndX=-610.709 EndY=116.573 EndZ=0
    g160: LineSegment StartX=-610.709 StartY=116.573 StartZ=0 EndX=-610.709 EndY=119.573 EndZ=0
    g161: LineSegment StartX=-610.709 StartY=119.573 StartZ=0 EndX=-640.709 EndY=119.573 EndZ=0
    g162: LineSegment StartX=-640.709 StartY=119.573 StartZ=0 EndX=-640.709 EndY=116.573 EndZ=0
    g163: LineSegment StartX=-640.709 StartY=116.573 StartZ=0 EndX=-660.709 EndY=116.573 EndZ=0
    g164: LineSegment StartX=-660.709 StartY=116.573 StartZ=0 EndX=-660.709 EndY=119.573 EndZ=0
    g165: LineSegment StartX=-660.709 StartY=119.573 StartZ=0 EndX=-690.709 EndY=119.573 EndZ=0
    g166: LineSegment StartX=-690.709 StartY=119.573 StartZ=0 EndX=-690.709 EndY=116.573 EndZ=0
    g167: LineSegment StartX=-690.709 StartY=116.573 StartZ=0 EndX=-720.709 EndY=116.573 EndZ=0
    g168: LineSegment StartX=-897.123 StartY=325.718 StartZ=0 EndX=-758.123 EndY=325.718 EndZ=0
    g169: LineSegment StartX=-902.623 StartY=265.718 StartZ=0 EndX=-752.623 EndY=265.718 EndZ=0
    g170: Circle CenterX=-892.123 CenterY=315.718 CenterZ=0 NormalX=0 NormalY=0 NormalZ=1 AngleXU=0 Radius=1.6
    g171: Circle CenterX=-874.223 CenterY=315.718 CenterZ=0 NormalX=0 NormalY=0 NormalZ=1 AngleXU=0 Radius=1.6
    g172: Circle CenterX=-781.023 CenterY=315.718 CenterZ=0 NormalX=0 NormalY=0 NormalZ=1 AngleXU=0 Radius=1.6
    g173: Circle CenterX=-763.123 CenterY=315.718 CenterZ=0 NormalX=0 NormalY=0 NormalZ=1 AngleXU=0 Radius=1.6
    g174: LineSegment StartX=-897.123 StartY=325.718 StartZ=0 EndX=-897.123 EndY=268.718 EndZ=0
    g175: LineSegment StartX=-897.123 StartY=268.718 StartZ=0 EndX=-902.623 EndY=268.718 EndZ=0
    g176: LineSegment StartX=-902.623 StartY=268.718 StartZ=0 EndX=-902.623 EndY=265.718 EndZ=0
    g177: LineSegment StartX=-758.123 StartY=325.718 StartZ=0 EndX=-758.123 EndY=268.718 EndZ=0
    g178: LineSegment StartX=-758.123 StartY=268.718 StartZ=0 EndX=-752.623 EndY=268.718 EndZ=0
    g179: LineSegment StartX=-752.623 StartY=268.718 StartZ=0 EndX=-752.623 EndY=265.718 EndZ=0
    g180: LineSegment StartX=-894.724 StartY=239.556 StartZ=0 EndX=-755.724 EndY=239.556 EndZ=0
    g181: LineSegment StartX=-894.724 StartY=239.556 StartZ=0 EndX=-894.724 EndY=179.556 EndZ=0
    g182: LineSegment StartX=-894.724 StartY=179.556 StartZ=0 EndX=-755.724 EndY=179.556 EndZ=0
    g183: LineSegment StartX=-755.724 StartY=239.556 StartZ=0 EndX=-755.724 EndY=179.556 EndZ=0
    g184: Circle CenterX=-889.724 CenterY=229.556 CenterZ=0 NormalX=0 NormalY=0 NormalZ=1 AngleXU=0 Radius=1.6
    g185: Circle CenterX=-871.824 CenterY=229.556 CenterZ=0 NormalX=0 NormalY=0 NormalZ=1 AngleXU=0 Radius=1.6
    g186: Circle CenterX=-889.724 CenterY=189.556 CenterZ=0 NormalX=0 NormalY=0 NormalZ=1 AngleXU=0 Radius=1.6
    g187: Circle CenterX=-871.824 CenterY=189.556 CenterZ=0 NormalX=0 NormalY=0 NormalZ=1 AngleXU=0 Radius=1.6
    g188: Circle CenterX=-778.624 CenterY=229.556 CenterZ=0 NormalX=0 NormalY=0 NormalZ=1 AngleXU=0 Radius=1.6
    g189: Circle CenterX=-760.724 CenterY=229.556 CenterZ=0 NormalX=0 NormalY=0 NormalZ=1 AngleXU=0 Radius=1.6
    g190: Circle CenterX=-778.624 CenterY=189.556 CenterZ=0 NormalX=0 NormalY=0 NormalZ=1 AngleXU=0 Radius=1.6
    g191: Circle CenterX=-760.724 CenterY=189.556 CenterZ=0 NormalX=0 NormalY=0 NormalZ=1 AngleXU=0 Radius=1.6
  constraints (558):
    c: Coincident(g0,g9)
    c: Coincident(g10,g9)
    c: Coincident(g1,g0)
    c: Coincident(g11,g10)
    c: Coincident(g1,g2)
    c: Coincident(g11,g12)
    c: Coincident(g3,g2)
    c: Coincident(g3,g4)
    c: Coincident(g13,g14)
    c: Coincident(g13,g12)
    c: Coincident(g5,g4)
    c: Coincident(g15,g14)
    c: Coincident(g15,g16)
    c: Coincident(g5,g6)
    c: Coincident(g6,g7)
    c: Coincident(g7,g8)
    c: Coincident(g17,g18)
    c: Coincident(g16,g17)
    c: Coincident(g8,g19)
    c: Coincident(g20,g19)
    c: Coincident(g21,g20)
    c: Coincident(g21,g22)
    c: Coincident(g18,g23)
    c: Coincident(g22,g23)
    c: Angle(g21) = 0
    c: Parallel(g21,g19)
    c: Parallel(g19,g23)
    c: Parallel(g23,g17)
    c: Parallel(g17,g7)
    c: Parallel(g7,g5)
    c: Parallel(g5,g15)
    c: Parallel(g15,g13)
    c: Parallel(g13,g3)
    c: Parallel(g3,g1)
    c: Parallel(g1,g11)
    c: Parallel(g11,g9)
    c: Perpendicular(g18,g21)
    c: Parallel(g18,g22)
    c: Parallel(g22,g20)
    c: Parallel(g20,g8)
    c: Parallel(g8,g6)
    c: Parallel(g6,g16)
    c: Parallel(g16,g14)
    c: Parallel(g14,g4)
    c: Parallel(g4,g2)
    c: Parallel(g2,g12)
    c: Parallel(g12,g10)
    c: Parallel(g10,g0)
    c: DistanceX(g11,g11) = 3
    c: DistanceX(g1,g1) = 3
    c: DistanceX(g5,g5) = 3
    c: DistanceX(g15,g15) = 3
    c: DistanceX(g19,g19) = 3
    c: DistanceX(g23,g23) = 3
    c: DistanceX(g4,g7) = 0
    c: DistanceX(g17,g14) = 0
    c: DistanceX(g0,g3) = 0
    c: DistanceX(g13,g10) = 0
    c: DistanceY(g0,g0) = 27
    c: DistanceY(g0,g10) = 0
    c: DistanceY(g3,g13) = 0
    c: DistanceY(g2,g2) = 30
    c: DistanceY(g4,g14) = 0
    c: DistanceY(g4,g4) = 22
    c: DistanceY(g6,g6) = 30
    c: DistanceY(g17,g7) = 0
    c: DistanceY(g8,g8) = 33.1
    c: DistanceY(g19,g22) = 0
    c: DistanceY(g20,g20) = 3
    c: DistanceX(g9,g9) = 49
    c: Coincident(g24,g25)
    c: Coincident(g47,g24)
    c: Coincident(g46,g47)
    c: Coincident(g46,g45)
    c: Coincident(g49,g48)
    c: Coincident(g48,g51)
    c: Coincident(g26,g25)
    c: Coincident(g26,g27)
    c: Coincident(g28,g27)
    c: Coincident(g28,g29)
    c: Coincident(g30,g29)
    c: Coincident(g30,g31)
    c: Coincident(g44,g45)
    c: Coincident(g44,g43)
    c: Coincident(g42,g43)
    c: Coincident(g42,g41)
    c: Coincident(g50,g51)
    c: Coincident(g50,g49)
    c: Coincident(g40,g41)
    c: Coincident(g40,g39)
    c: Coincident(g32,g33)
    c: Coincident(g32,g31)
    c: Coincident(g33,g34)
    c: Coincident(g34,g35)
    c: Coincident(g35,g36)
    c: Coincident(g37,g36)
    c: Coincident(g38,g37)
    c: Coincident(g39,g38)
    c: Angle(g36) = 0
    c: Perpendicular(g37,g36)
    c: Parallel(g36,g38)
    c: Parallel(g38,g34)
    c: Parallel(g34,g50)
    c: Parallel(g50,g40)
    c: Parallel(g40,g32)
    c: Parallel(g32,g30)
    c: Parallel(g30,g42)
    c: Parallel(g42,g44)
    c: Parallel(g44,g28)
    c: Parallel(g28,g26)
    c: Parallel(g26,g46)
    c: Parallel(g46,g24)
    c: Parallel(g24,g48)
    c: Parallel(g37,g35)
    c: Parallel(g35,g33)
    c: Parallel(g33,g39)
    c: Parallel(g39,g49)
    c: Parallel(g49,g51)
    c: Parallel(g51,g31)
    c: Parallel(g31,g41)
    c: Parallel(g41,g29)
    c: Parallel(g29,g43)
    c: Parallel(g43,g45)
    c: Parallel(g45,g27)
    c: Parallel(g27,g25)
    c: Parallel(g25,g47)
    c: DistanceX(g48,g48) = 3
    c: DistanceX(g26,g26) = 3
    c: DistanceX(g46,g46) = 3
    c: DistanceX(g28,g25) = 0
    c: DistanceX(g43,g46) = 0
    c: DistanceY(g25,g46) = 0
    c: DistanceX(g30,g30) = 3
    c: DistanceX(g42,g42) = 3
    c: DistanceY(g42,g29) = 0
    c: DistanceX(g32,g29) = 0
    c: DistanceX(g39,g42) = 0
    c: DistanceY(g39,g32) = 0
    c: DistanceY(g43,g28) = 0
    c: DistanceX(g34,g34) = 3
    c: DistanceX(g38,g38) = 3
    c: DistanceY(g35,g35) = 3
    c: DistanceY(g37,g34) = 0
    c: DistanceX(g24,g24) = 49
    c: DistanceY(g25,g25) = 27
    c: DistanceY(g27,g27) = 30
    c: DistanceY(g29,g29) = 22
    c: DistanceY(g31,g31) = 30
    c: DistanceY(g33,g33) = 33.1
    c: DistanceY(g48,g24) = 15
    c: DistanceX(g48,g24) = 5
    c: Coincident(g54,g55)
    c: Coincident(g52,g55)
    c: Coincident(g52,g53)
    c: Coincident(g54,g53)
    c: Parallel(g54,g52)
    c: Parallel(g52,g36)
    c: Parallel(g53,g55)
    c: Parallel(g55,g39)
    c: DistanceY(g55,g55) = 3
    c: DistanceX(g54,g54) = 20
    c: DistanceX(g33,g53) = 10
    c: DistanceY(g33,g52) = 15
    c: DistanceY(g52,g50) = 0
    c: Coincident(g56,g57)
    c: Coincident(g56,g59)
    c: Coincident(g58,g57)
    c: Coincident(g58,g61)
    c: Coincident(g60,g62)
    c: Coincident(g60,g59)
    c: Coincident(g63,g61)
    c: Coincident(g64,g62)
    c: Coincident(g64,g67)
    c: Coincident(g63,g65)
    c: Coincident(g66,g65)
    c: Coincident(g68,g67)
    c: Coincident(g68,g73)
    c: Coincident(g66,g69)
    c: Coincident(g74,g73)
    c: Coincident(g70,g69)
    c: Coincident(g70,g71)
    c: Coincident(g75,g74)
    c: Coincident(g71,g72)
    c: Coincident(g72,g75)
    c: DistanceX(g56,g56) = 30
    c: Angle(g56) = 0
    c: Perpendicular(g59,g56)
    c: Parallel(g56,g58)
    c: Parallel(g58,g60)
    c: Parallel(g60,g63)
    c: Parallel(g63,g64)
    c: Parallel(g64,g66)
    c: Parallel(g66,g68)
    c: Parallel(g68,g70)
    c: Parallel(g70,g74)
    c: Parallel(g74,g72)
    c: Parallel(g59,g57)
    c: Parallel(g57,g61)
    c: Parallel(g61,g62)
    c: Parallel(g62,g65)
    c: Parallel(g65,g67)
    c: Parallel(g67,g69)
    c: Parallel(g69,g73)
    c: Parallel(g73,g71)
    c: Parallel(g71,g75)
    c: DistanceY(g60,g58) = 0
    c: DistanceY(g62,g61) = 0
    c: DistanceY(g68,g66) = 0
    c: DistanceY(g73,g69) = 0
    c: DistanceX(g58,g58) = 3
    c: DistanceX(g60,g60) = 3
    c: DistanceX(g63,g63) = 3
    c: DistanceX(g64,g64) = 3
    c: DistanceX(g61,g66) = 0
    c: DistanceX(g68,g62) = 0
    c: DistanceX(g70,g70) = 3
    c: DistanceX(g74,g74) = 3
    c: DistanceY(g57,g57) = 27
    c: DistanceY(g61,g61) = 30
    c: DistanceY(g65,g65) = 22
    c: DistanceY(g69,g69) = 30
    c: DistanceY(g71,g71) = 33.1
    c: Coincident(g100,g101)
    c: Coincident(g102,g101)
    c: Coincident(g102,g103)
    c: Coincident(g76,g103)
    c: Coincident(g77,g76)
    c: Coincident(g77,g78)
    c: Coincident(g79,g78)
    c: Coincident(g79,g80)
    c: Coincident(g100,g99)
    c: Coincident(g98,g99)
    c: Coincident(g97,g98)
    c: Coincident(g97,g96)
    c: Coincident(g95,g96)
    c: Coincident(g95,g94)
    c: Coincident(g93,g94)
    c: Coincident(g81,g80)
    c: Coincident(g81,g82)
    c: Coincident(g83,g82)
    c: Coincident(g83,g84)
    c: Coincident(g85,g84)
    c: Coincident(g86,g85)
    c: Coincident(g86,g87)
    c: Coincident(g88,g87)
    c: Coincident(g88,g89)
    c: Coincident(g89,g90)
    c: Coincident(g91,g90)
    c: Coincident(g91,g92)
    c: Coincident(g93,g92)
    c: Angle(g94) = 3.14159
    c: Perpendicular(g93,g94)
    c: Parallel(g94,g92)
    c: Parallel(g92,g90)
    c: Parallel(g90,g88)
    c: Parallel(g88,g86)
    c: Parallel(g86,g84)
    c: Parallel(g84,g82)
    c: Parallel(g82,g80)
    c: Parallel(g80,g78)
    c: Parallel(g78,g76)
    c: Parallel(g76,g102)
    c: Parallel(g102,g100)
    c: Parallel(g100,g98)
    c: Parallel(g98,g96)
    c: Parallel(g93,g91)
    c: Parallel(g91,g89)
    c: Parallel(g89,g87)
    c: Parallel(g87,g85)
    c: Parallel(g85,g83)
    c: Parallel(g83,g81)
    c: Parallel(g81,g79)
    c: Parallel(g79,g77)
    c: Parallel(g77,g103)
    c: Parallel(g103,g101)
    c: Parallel(g101,g99)
    c: Parallel(g99,g97)
    c: Parallel(g97,g95)
    c: DistanceY(g94,g97) = 0
    c: DistanceY(g90,g93) = 0
    c: DistanceY(g83,g80) = 0
    c: DistanceY(g79,g76) = 0
    c: DistanceX(g102,g99) = 0
    c: DistanceX(g85,g88) = 0
    c: DistanceY(g95,g95) = 3
    c: DistanceY(g93,g93) = 3
    c: DistanceX(g88,g88) = 3
    c: DistanceY(g81,g81) = 3
    c: DistanceY(g79,g79) = 3
    c: DistanceX(g100,g100) = 3
    c: DistanceY(g101,g101) = 20
    c: DistanceY(g87,g87) = 20
    c: DistanceX(g78,g78) = 30
    c: Equal(g78,g82)
    c: Equal(g82,g92)
    c: Equal(g92,g96)
    c: DistanceY(g103,g103) = 10
    c: DistanceY(g85,g85) = 10
    c: DistanceY(g76,g98) = 49
    c: DistanceX(g76,g76) = 30
    c: DistanceX(g94,g94) = 20
    c: DistanceX(g98,g98) = 30
    c: DistanceX(g90,g90) = 30
    c: DistanceX(g84,g84) = 30
    c: Angle(g108) = 0
    c: Perpendicular(g115,g108)
    c: Coincident(g104,g142)
    c: Coincident(g141,g142)
    c: Coincident(g141,g140)
    c: Coincident(g139,g140)
    c: Coincident(g139,g138)
    c: Coincident(g138,g137)
    c: Coincident(g137,g136)
    c: Coincident(g136,g135)
    c: Coincident(g134,g135)
    c: Coincident(g134,g133)
    c: Coincident(g133,g132)
    c: Coincident(g131,g132)
    c: Coincident(g131,g130)
    c: Coincident(g129,g130)
    c: Coincident(g129,g128)
    c: Coincident(g127,g128)
    c: Coincident(g127,g126)
    c: Coincident(g125,g126)
    c: Coincident(g125,g124)
    c: Coincident(g124,g123)
    c: Coincident(g122,g123)
    c: Coincident(g118,g122)
    c: Coincident(g118,g117)
    c: Coincident(g117,g116)
    c: Coincident(g116,g115)
    c: Coincident(g115,g114)
    c: Coincident(g114,g113)
    c: Coincident(g112,g113)
    c: Coincident(g112,g121)
    c: Coincident(g121,g120)
    c: Coincident(g119,g120)
    c: Coincident(g147,g119)
    c: Coincident(g111,g147)
    c: Coincident(g111,g110)
    c: Coincident(g109,g110)
    c: Coincident(g109,g108)
    c: Coincident(g108,g107)
    c: Coincident(g107,g106)
    c: Coincident(g105,g106)
    c: Coincident(g146,g105)
    c: Coincident(g146,g145)
    c: Coincident(g145,g144)
    c: Coincident(g143,g144)
    c: Coincident(g104,g143)
    c: Parallel(g115,g113)
    c: Parallel(g113,g121)
    c: Parallel(g121,g119)
    c: Parallel(g119,g111)
    c: Parallel(g111,g109)
    c: Parallel(g109,g107)
    c: Parallel(g107,g105)
    c: Parallel(g105,g145)
    c: Parallel(g145,g143)
    c: Parallel(g143,g142)
    c: Parallel(g142,g140)
    c: Parallel(g140,g138)
    c: Parallel(g138,g136)
    c: Parallel(g136,g134)
    c: Parallel(g134,g132)
    c: Parallel(g132,g130)
    c: Parallel(g130,g128)
    c: Parallel(g128,g126)
    c: Parallel(g126,g124)
    c: Parallel(g124,g122)
    c: Parallel(g122,g117)
    c: Parallel(g112,g114)
    c: Parallel(g114,g120)
    c: Parallel(g120,g147)
    c: Parallel(g147,g110)
    c: Parallel(g110,g108)
    c: Parallel(g108,g106)
    c: Parallel(g106,g146)
    c: Parallel(g146,g144)
    c: Parallel(g144,g104)
    c: Parallel(g104,g141)
    c: Parallel(g141,g139)
    c: Parallel(g139,g137)
    c: Parallel(g137,g135)
    c: Parallel(g135,g133)
    c: Parallel(g133,g131)
    c: Parallel(g131,g129)
    c: Parallel(g129,g127)
    c: Parallel(g127,g125)
    c: Parallel(g125,g123)
    c: Parallel(g123,g118)
    c: Parallel(g118,g116)
    c: DistanceX(g113,g116) = 0
    c: DistanceX(g116,g116) = 3
    c: DistanceX(g139,g139) = 3
    c: DistanceX(g138,g141) = 0
    c: DistanceY(g138,g138) = 3
    c: DistanceY(g142,g142) = 3
    c: DistanceY(g143,g143) = 3
    c: DistanceY(g145,g104) = 0
    c: DistanceY(g136,g136) = 3
    c: DistanceY(g136,g133) = 0
    c: DistanceX(g135,g135) = 3
    c: DistanceX(g144,g144) = 3
    c: DistanceY(g124,g124) = 3
    c: DistanceY(g124,g118) = 0
    c: DistanceX(g123,g123) = 3
    c: DistanceX(g120,g120) = 3
    c: DistanceY(g119,g119) = 3
    c: DistanceY(g112,g119) = 0
    c: DistanceY(g117,g117) = 3
    c: DistanceY(g113,g113) = 3
    c: DistanceX(g131,g131) = 30
    c: DistanceX(g127,g127) = 30
    c: DistanceX(g129,g129) = 20
    c: DistanceX(g133,g133) = 30
    c: DistanceX(g125,g125) = 30
    c: DistanceX(g124,g115) = 30
    c: DistanceX(g119,g114) = 30
    c: DistanceY(g132,g132) = 3
    c: DistanceY(g128,g128) = 3
    c: DistanceY(g129,g132) = 0
    c: DistanceY(g125,g128) = 0
    c: DistanceX(g139,g133) = 30
    c: DistanceX(g140,g144) = 30
    c: DistanceY(g105,g105) = 3
    c: DistanceY(g109,g109) = 3
    c: DistanceY(g105,g107) = 0
    c: DistanceY(g111,g108) = 0
    c: DistanceX(g146,g146) = 10
    c: DistanceX(g147,g147) = 10
    c: DistanceX(g110,g110) = 40
    c: DistanceX(g106,g106) = 40
    c: DistanceY(g104,g137) = 49
    c: Coincident(g148,g149)
    c: Coincident(g148,g167)
    c: Coincident(g166,g167)
    c: Coincident(g166,g165)
    c: Coincident(g150,g149)
    c: Coincident(g150,g151)
    c: Coincident(g152,g151)
    c: Coincident(g152,g153)
    c: Coincident(g154,g153)
    c: Coincident(g154,g155)
    c: Coincident(g156,g155)
    c: Coincident(g156,g157)
    c: Coincident(g157,g158)
    c: Coincident(g158,g159)
    c: Coincident(g160,g159)
    c: Coincident(g160,g161)
    c: Coincident(g162,g161)
    c: Coincident(g163,g162)
    c: Coincident(g164,g163)
    c: Coincident(g164,g165)
    c: Angle(g165) = 3.14159
    c: Perpendicular(g158,g165)
    c: Parallel(g165,g151)
    c: Parallel(g151,g149)
    c: Parallel(g149,g167)
    c: Parallel(g167,g163)
    c: Parallel(g163,g153)
    c: Parallel(g153,g155)
    c: Parallel(g155,g161)
    c: Parallel(g161,g159)
    c: Parallel(g159,g157)
    c: Parallel(g158,g156)
    c: Parallel(g156,g160)
    c: Parallel(g160,g162)
    c: Parallel(g162,g154)
    c: Parallel(g154,g164)
    c: Parallel(g164,g152)
    c: Parallel(g152,g166)
    c: Parallel(g166,g150)
    c: Parallel(g150,g148)
    c: DistanceY(g152,g152) = 3
    c: DistanceY(g154,g154) = 3
    c: DistanceY(g149,g152) = 0
    c: DistanceY(g156,g153) = 0
    c: DistanceY(g162,g162) = 3
    c: DistanceY(g164,g164) = 3
    c: DistanceY(g159,g162) = 0
    c: DistanceY(g166,g163) = 0
    c: DistanceX(g151,g151) = 30
    c: DistanceX(g155,g155) = 30
    c: DistanceX(g153,g153) = 20
    c: DistanceX(g149,g149) = 30
    c: DistanceX(g157,g157) = 30
    c: DistanceX(g161,g161) = 30
    c: DistanceX(g165,g165) = 30
    c: DistanceX(g159,g159) = 30
    c: DistanceX(g167,g167) = 30
    c: DistanceY(g148,g148) = 15
    c: Angle(g169) = 0
    c: Parallel(g169,g168)
    c: DistanceY(g169,g168) = 60
    c: DistanceX(g168,g168) = 139
    c: Radius(g170) = 1.6
    c: Equal(g171,g172)
    c: DistanceY(g170,g171) = 0
    c: DistanceX(g170,g171) = 17.9
    c: DistanceY(g172,g173) = 0
    c: DistanceX(g172,g173) = 17.9
    c: DistanceY(g170,g168) = 10
    c: DistanceX(g168,g170) = 5
    c: DistanceY(g173,g168) = 10
    c: DistanceX(g173,g168) = 5
    c: Coincident(g168,g174)
    c: Coincident(g174,g175)
    c: Coincident(g175,g176)
    c: Coincident(g176,g169)
    c: Coincident(g168,g177)
    c: Coincident(g177,g178)
    c: Coincident(g178,g179)
    c: Coincident(g179,g169)
    c: DistanceX(g169,g169) = 150
    c: DistanceX(g175,g175) = 5.5
    c: DistanceX(g178,g178) = 5.5
    c: Perpendicular(g177,g169)
    c: Parallel(g177,g179)
    c: Parallel(g179,g174)
    c: Parallel(g175,g169)
    c: Parallel(g169,g178)
    c: DistanceY(g176,g176) = 3
    c: DistanceY(g179,g179) = 3
    c: Coincident(g182,g183)
    c: Coincident(g180,g183)
    c: Coincident(g180,g181)
    c: Coincident(g182,g181)
    c: Angle(g182) = 0
    c: Perpendicular(g183,g182)
    c: Parallel(g182,g180)
    c: Parallel(g183,g181)
    c: DistanceX(g180,g180) = 139
    c: DistanceY(g181,g181) = 60
    c: Radius(g184) = 1.6
    c: Equal(g184,g185)
    c: Equal(g185,g186)
    c: Equal(g186,g187)
    c: Equal(g187,g190)
    c: Equal(g190,g191)
    c: Equal(g191,g189)
    c: Equal(g189,g188)
    c: DistanceY(g184,g185) = 0
    c: DistanceY(g186,g187) = 0
    c: DistanceY(g188,g189) = 0
    c: DistanceY(g190,g191) = 0
    c: DistanceX(g184,g185) = 17.9
    c: DistanceX(g186,g187) = 17.9
    c: DistanceX(g188,g189) = 17.9
    c: DistanceX(g190,g191) = 17.9
    c: DistanceX(g180,g184) = 5
    c: DistanceY(g184,g180) = 10
    c: DistanceX(g181,g186) = 5
    c: DistanceY(g181,g186) = 10
    c: DistanceX(g191,g182) = 5
    c: DistanceY(g182,g191) = 10
    c: DistanceX(g189,g180) = 5
    c: DistanceY(g189,g180) = 10
FEATURE [App::Part] Part002
  Origin = -> Origin002
FEATURE [Sketcher::SketchObject] Sketch002
  sketch-geometry (14):
    g0: LineSegment StartX=-1045.45 StartY=151.998 StartZ=0 EndX=-936.45 EndY=151.998 EndZ=0
    g1: LineSegment StartX=-1045.45 StartY=151.998 StartZ=0 EndX=-1045.45 EndY=127.998 EndZ=0
    g2: LineSegment StartX=-1045.45 StartY=127.998 StartZ=0 EndX=-1053.45 EndY=127.998 EndZ=0
    g3: LineSegment StartX=-1053.45 StartY=127.998 StartZ=0 EndX=-1053.45 EndY=124.998 EndZ=0
    g4: LineSegment StartX=-1053.45 StartY=124.998 StartZ=0 EndX=-1045.45 EndY=124.998 EndZ=0
    g5: LineSegment StartX=-1045.45 StartY=124.998 StartZ=0 EndX=-1045.45 EndY=121.998 EndZ=0
    g6: LineSegment StartX=-1045.45 StartY=121.998 StartZ=0 EndX=-1015.45 EndY=121.998 EndZ=0
    g7: LineSegment StartX=-1015.45 StartY=121.998 StartZ=0 EndX=-1015.45 EndY=124.998 EndZ=0
    g8: LineSegment StartX=-1015.45 StartY=124.998 StartZ=0 EndX=-966.45 EndY=124.998 EndZ=0
    g9: LineSegment StartX=-966.45 StartY=124.998 StartZ=0 EndX=-966.45 EndY=121.998 EndZ=0
    g10: LineSegment StartX=-966.45 StartY=121.998 StartZ=0 EndX=-936.45 EndY=121.998 EndZ=0
    g11: LineSegment StartX=-936.45 StartY=151.998 StartZ=0 EndX=-936.45 EndY=121.998 EndZ=0
    g12: Circle CenterX=-999.9 CenterY=141.998 CenterZ=0 NormalX=0 NormalY=0 NormalZ=1 AngleXU=0 Radius=1.6
    g13: Circle CenterX=-982 CenterY=141.998 CenterZ=0 NormalX=0 NormalY=0 NormalZ=1 AngleXU=0 Radius=1.6
  constraints (40):
    c: Coincident(g2,g1)
    c: Coincident(g2,g3)
    c: Coincident(g4,g3)
    c: Coincident(g5,g4)
    c: Coincident(g5,g6)
    c: Coincident(g7,g6)
    c: Coincident(g8,g7)
    c: Coincident(g8,g9)
    c: Coincident(g10,g9)
    c: Coincident(g0,g1)
    c: Coincident(g0,g11)
    c: Coincident(g10,g11)
    c: Angle(g8) = 0
    c: Perpendicular(g7,g8)
    c: Parallel(g8,g6)
    c: Parallel(g6,g4)
    c: Parallel(g4,g2)
    c: Parallel(g2,g0)
    c: Parallel(g0,g10)
    c: Parallel(g7,g9)
    c: Parallel(g9,g3)
    c: Parallel(g3,g5)
    c: Parallel(g5,g1)
    c: Parallel(g1,g11)
    c: Radius(g12) = 1.6
    c: Equal(g12,g13)
    c: DistanceY(g12,g13) = 0
    c: DistanceX(g12,g13) = 17.9
    c: DistanceX(g2,g2) = 8
    c: DistanceX(g1,g4) = 0
    c: DistanceY(g3,g3) = 3
    c: DistanceY(g5,g5) = 3
    c: DistanceY(g7,g7) = 3
    c: DistanceY(g9,g6) = 0
    c: DistanceY(g5,g0) = 30
    c: DistanceX(g0,g0) = 109
    c: DistanceX(g6,g6) = 30
    c: DistanceX(g10,g10) = 30
    c: DistanceY(g12,g0) = 10
    c: DistanceX(g0,g12) = 45.55
